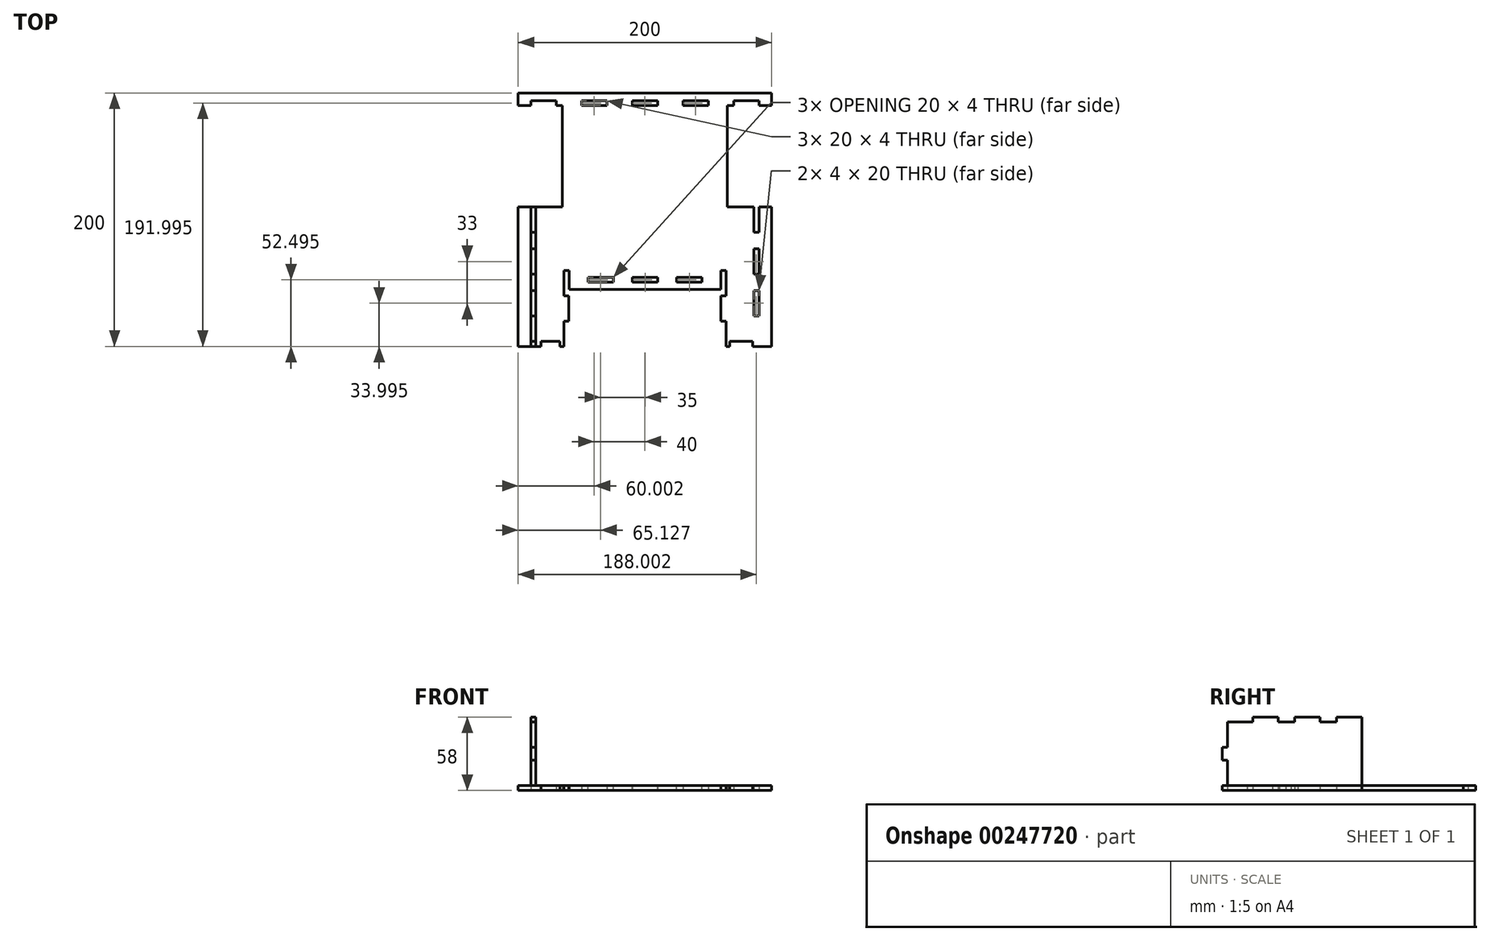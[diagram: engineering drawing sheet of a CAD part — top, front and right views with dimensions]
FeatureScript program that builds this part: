
annotation { "Feature Type Name" : "Feature", "Feature Type Description" : "" }
export const myFeature = defineFeature(function(context is Context, id is Id, definition is map)
    precondition{}
    {
        {
            var Q0;
            Q0=qCreatedBy(makeId("Top.planeOp"),FACE);
            var sketch = newSketch(context, id + "F0", { "sketchPlane" : qUnion([Q0])});
            skLineSegment(sketch, "E0.bottom", {"start": v(-157.98, 33.52) * mm, "end": v(42.02, 33.52) * mm});
            skLineSegment(sketch, "E0.top", {"start": v(-157.98, -166.48) * mm, "end": v(42.02, -166.48) * mm});
            skLineSegment(sketch, "E0.left", {"start": v(-157.98, 33.52) * mm, "end": v(-157.98, -166.48) * mm});
            skLineSegment(sketch, "E0.right", {"start": v(42.02, 33.52) * mm, "end": v(42.02, -166.48) * mm});
            skPoint(sketch, "E0.middle", {"position": v(-57.98, -66.48) * mm});
            skLineSegment(sketch, "E1", {"start": v(-57.98, -166.48) * mm, "end": v(-57.98, 18.52) * mm, "construction": true});
            skLineSegment(sketch, "E2", {"start": v(-57.98, 33.52) * mm, "end": v(-57.98, 27.52) * mm, "construction": true});
            skLineSegment(sketch, "E3.direction2", {"start": v(-47.98, 18.52) * mm, "end": v(-47.15, -161.48) * mm, "construction": true});
            skLineSegment(sketch, "E4", {"start": v(42.02, -66.48) * mm, "end": v(32.02, -66.48) * mm, "construction": true});
            skLineSegment(sketch, "E5", {"start": v(32.02, -66.48) * mm, "end": v(42.02, -66.48) * mm, "construction": true});
            skLineSegment(sketch, "E6.top", {"start": v(32.02, -76.48) * mm, "end": v(28.02, -76.48) * mm});
            skLineSegment(sketch, "E6.left", {"start": v(32.02, -66.48) * mm, "end": v(32.02, -76.48) * mm});
            skLineSegment(sketch, "E6.right", {"start": v(28.02, -66.48) * mm, "end": v(28.02, -76.48) * mm});
            skLineSegment(sketch, "E7.MirrorCS", {"start": v(28.02, -66.48) * mm, "end": v(28.02, -56.48) * mm});
            skLineSegment(sketch, "E8.MirrorCS", {"start": v(32.02, -66.48) * mm, "end": v(32.02, -56.48) * mm});
            skLineSegment(sketch, "E9.MirrorCS", {"start": v(32.02, -56.48) * mm, "end": v(28.02, -56.48) * mm});
            skLineSegment(sketch, "E10.trimOffspring", {"start": v(28.02, -66.48) * mm, "end": v(-157.98, -66.48) * mm, "construction": true});
            skLineSegment(sketch, "E11.direction1", {"start": v(28.02, -66.48) * mm, "end": v(52.02, -66.48) * mm, "construction": true});
            skLineSegment(sketch, "E11.direction2", {"start": v(28.02, -66.48) * mm, "end": v(28.02, -33.48) * mm, "construction": true});
            skLineSegment(sketch, "E12.MirrorCS", {"start": v(32.02, -99.48) * mm, "end": v(32.02, -109.48) * mm});
            skLineSegment(sketch, "E13.MirrorCS", {"start": v(32.02, -89.48) * mm, "end": v(28.02, -89.48) * mm});
            skLineSegment(sketch, "E14.MirrorCS", {"start": v(28.02, -99.48) * mm, "end": v(28.02, -89.48) * mm});
            skLineSegment(sketch, "E15.MirrorCS", {"start": v(28.02, -99.48) * mm, "end": v(28.02, -109.48) * mm});
            skLineSegment(sketch, "E16.MirrorCS", {"start": v(32.02, -99.48) * mm, "end": v(32.02, -89.48) * mm});
            skLineSegment(sketch, "E17.MirrorCS", {"start": v(32.02, -109.48) * mm, "end": v(28.02, -109.48) * mm});
            skLineSegment(sketch, "E18.MirrorCS", {"start": v(-147.98, -56.48) * mm, "end": v(-143.98, -56.48) * mm});
            skLineSegment(sketch, "E19.MirrorCS", {"start": v(-147.98, -99.48) * mm, "end": v(-147.98, -89.48) * mm});
            skLineSegment(sketch, "E20.MirrorCS", {"start": v(-147.98, -89.48) * mm, "end": v(-143.98, -89.48) * mm});
            skLineSegment(sketch, "E21.MirrorCS", {"start": v(-147.98, -76.48) * mm, "end": v(-143.98, -76.48) * mm});
            skLineSegment(sketch, "E22.MirrorCS", {"start": v(-147.98, -109.48) * mm, "end": v(-143.98, -109.48) * mm});
            skLineSegment(sketch, "E23.MirrorCS", {"start": v(-143.98, -99.48) * mm, "end": v(-143.98, -89.48) * mm});
            skLineSegment(sketch, "E24.MirrorCS", {"start": v(-143.98, -66.48) * mm, "end": v(-143.98, -56.48) * mm});
            skLineSegment(sketch, "E25.MirrorCS", {"start": v(-147.98, -99.48) * mm, "end": v(-147.98, -109.48) * mm});
            skLineSegment(sketch, "E26.MirrorCS", {"start": v(-143.98, -66.48) * mm, "end": v(-143.98, -33.48) * mm, "construction": true});
            skLineSegment(sketch, "E27.MirrorCS", {"start": v(-147.98, -66.48) * mm, "end": v(-147.98, -56.48) * mm});
            skLineSegment(sketch, "E28.MirrorCS", {"start": v(-143.98, -99.48) * mm, "end": v(-143.98, -109.48) * mm});
            skLineSegment(sketch, "E29.MirrorCS", {"start": v(-143.98, -66.48) * mm, "end": v(-143.98, -76.48) * mm});
            skLineSegment(sketch, "E30.MirrorCS", {"start": v(-147.98, -66.48) * mm, "end": v(-147.98, -76.48) * mm});
            skLineSegment(sketch, "E31.bottom", {"start": v(-57.98, 23.52) * mm, "end": v(-47.98, 23.52) * mm});
            skLineSegment(sketch, "E31.top", {"start": v(-57.98, 27.52) * mm, "end": v(-47.98, 27.52) * mm});
            skLineSegment(sketch, "E31.right", {"start": v(-47.98, 23.52) * mm, "end": v(-47.98, 27.52) * mm});
            skLineSegment(sketch, "E32.MirrorCS", {"start": v(-57.98, 27.52) * mm, "end": v(-67.98, 27.52) * mm});
            skLineSegment(sketch, "E33.MirrorCS", {"start": v(-67.98, 23.52) * mm, "end": v(-67.98, 27.52) * mm});
            skLineSegment(sketch, "E34.MirrorCS", {"start": v(-57.98, 23.52) * mm, "end": v(-67.98, 23.52) * mm});
            skPoint(sketch, "E35.orphan", {"position": v(-57.98, 23.52) * mm});
            skLineSegment(sketch, "E36.1.0.0", {"start": v(-17.98, 23.52) * mm, "end": v(-27.98, 23.52) * mm});
            skLineSegment(sketch, "E36.1.0.1", {"start": v(-27.98, 23.52) * mm, "end": v(-27.98, 27.52) * mm});
            skLineSegment(sketch, "E36.1.0.2", {"start": v(-7.98, 23.52) * mm, "end": v(-7.98, 27.52) * mm});
            skLineSegment(sketch, "E36.1.0.3", {"start": v(-17.98, 23.52) * mm, "end": v(-7.98, 23.52) * mm});
            skLineSegment(sketch, "E36.1.0.4", {"start": v(-17.98, 27.52) * mm, "end": v(-27.98, 27.52) * mm});
            skLineSegment(sketch, "E36.1.0.5", {"start": v(-17.98, 27.52) * mm, "end": v(-7.98, 27.52) * mm});
            skPoint(sketch, "E36.1.0.6", {"position": v(-17.98, 23.52) * mm});
            skLineSegment(sketch, "E36.2.0.0", {"start": v(22.02, 23.52) * mm, "end": v(12.02, 23.52) * mm});
            skLineSegment(sketch, "E36.2.0.1", {"start": v(12.02, 23.52) * mm, "end": v(12.02, 27.52) * mm});
            skLineSegment(sketch, "E36.2.0.2", {"start": v(32.02, 23.52) * mm, "end": v(32.02, 27.52) * mm});
            skLineSegment(sketch, "E36.2.0.3", {"start": v(22.02, 23.52) * mm, "end": v(32.02, 23.52) * mm});
            skLineSegment(sketch, "E36.2.0.4", {"start": v(22.02, 27.52) * mm, "end": v(12.02, 27.52) * mm});
            skLineSegment(sketch, "E36.2.0.5", {"start": v(22.02, 27.52) * mm, "end": v(32.02, 27.52) * mm});
            skPoint(sketch, "E36.2.0.6", {"position": v(22.02, 23.52) * mm});
            skLineSegment(sketch, "E36.direction1", {"start": v(-67.98, 23.52) * mm, "end": v(-27.98, 23.52) * mm, "construction": true});
            skPoint(sketch, "E37.MirrorP", {"position": v(-97.98, 23.52) * mm});
            skLineSegment(sketch, "E38.MirrorCS", {"start": v(-137.98, 23.52) * mm, "end": v(-147.98, 23.52) * mm});
            skLineSegment(sketch, "E39.MirrorCS", {"start": v(-97.98, 23.52) * mm, "end": v(-107.98, 23.52) * mm});
            skLineSegment(sketch, "E40.MirrorCS", {"start": v(-107.98, 23.52) * mm, "end": v(-107.98, 27.52) * mm});
            skLineSegment(sketch, "E41.MirrorCS", {"start": v(-137.98, 23.52) * mm, "end": v(-127.98, 23.52) * mm});
            skLineSegment(sketch, "E42.MirrorCS", {"start": v(-97.98, 27.52) * mm, "end": v(-107.98, 27.52) * mm});
            skLineSegment(sketch, "E43.MirrorCS", {"start": v(-97.98, 27.52) * mm, "end": v(-87.98, 27.52) * mm});
            skLineSegment(sketch, "E44.MirrorCS", {"start": v(-137.98, 27.52) * mm, "end": v(-147.98, 27.52) * mm});
            skLineSegment(sketch, "E45.MirrorCS", {"start": v(-137.98, 27.52) * mm, "end": v(-127.98, 27.52) * mm});
            skLineSegment(sketch, "E46.MirrorCS", {"start": v(-147.98, 23.52) * mm, "end": v(-147.98, 27.52) * mm});
            skPoint(sketch, "E47.MirrorP", {"position": v(-137.98, 23.52) * mm});
            skLineSegment(sketch, "E48.MirrorCS", {"start": v(-87.98, 23.52) * mm, "end": v(-87.98, 27.52) * mm});
            skLineSegment(sketch, "E49.MirrorCS", {"start": v(-127.98, 23.52) * mm, "end": v(-127.98, 27.52) * mm});
            skLineSegment(sketch, "E50.MirrorCS", {"start": v(-97.98, 23.52) * mm, "end": v(-87.98, 23.52) * mm});
            skLineSegment(sketch, "E51.MirrorCS", {"start": v(-143.98, -66.48) * mm, "end": v(42.02, -66.48) * mm, "construction": true});
            skLineSegment(sketch, "E52.MirrorCS", {"start": v(-143.98, -132.48) * mm, "end": v(-143.98, -122.48) * mm});
            skLineSegment(sketch, "E53.MirrorCS", {"start": v(-143.98, -132.48) * mm, "end": v(-143.98, -142.48) * mm});
            skLineSegment(sketch, "E54.MirrorCS", {"start": v(-147.98, -142.48) * mm, "end": v(-143.98, -142.48) * mm});
            skLineSegment(sketch, "E55.MirrorCS", {"start": v(-147.98, -132.48) * mm, "end": v(-147.98, -122.48) * mm});
            skLineSegment(sketch, "E56.MirrorCS", {"start": v(-147.98, -122.48) * mm, "end": v(-143.98, -122.48) * mm});
            skLineSegment(sketch, "E57.MirrorCS", {"start": v(-147.98, -132.48) * mm, "end": v(-147.98, -142.48) * mm});
            skLineSegment(sketch, "E58.MirrorCS", {"start": v(32.02, -132.48) * mm, "end": v(32.02, -142.48) * mm});
            skLineSegment(sketch, "E59.MirrorCS", {"start": v(32.02, -132.48) * mm, "end": v(32.02, -122.48) * mm});
            skLineSegment(sketch, "E60.MirrorCS", {"start": v(32.02, -122.48) * mm, "end": v(28.02, -122.48) * mm});
            skLineSegment(sketch, "E61.MirrorCS", {"start": v(28.02, -132.48) * mm, "end": v(28.02, -142.48) * mm});
            skLineSegment(sketch, "E62.MirrorCS", {"start": v(32.02, -142.48) * mm, "end": v(28.02, -142.48) * mm});
            skLineSegment(sketch, "E63.MirrorCS", {"start": v(28.02, -132.48) * mm, "end": v(28.02, -122.48) * mm});
            skSolve(sketch);
        }
        {
            var Q0;
            Q0 = qSketchRegion(id + "F0", true);
            extrude(context, id + "F1", {"entities" : qUnion([Q0]), "depth" : 4 * mm});
        }
        {
            var Q0;
            Q0=makeQuery(id+"F1.opExtrude","CAP_FACE",FACE,{"disambiguationData":[OSD([sQuery(id+"F0.wireOp",EDGE,"E0.bottom"),sQuery(id+"F0.wireOp",EDGE,"E0.top"),sQuery(id+"F0.wireOp",EDGE,"E0.left"),sQuery(id+"F0.wireOp",EDGE,"E0.right"),sQuery(id+"F0.wireOp",EDGE,"E6.top"),sQuery(id+"F0.wireOp",EDGE,"E6.left"),sQuery(id+"F0.wireOp",EDGE,"E6.right"),sQuery(id+"F0.wireOp",EDGE,"E7.MirrorCS"),sQuery(id+"F0.wireOp",EDGE,"E8.MirrorCS"),sQuery(id+"F0.wireOp",EDGE,"E9.MirrorCS"),sQuery(id+"F0.wireOp",EDGE,"E12.MirrorCS"),sQuery(id+"F0.wireOp",EDGE,"E13.MirrorCS"),sQuery(id+"F0.wireOp",EDGE,"E14.MirrorCS"),sQuery(id+"F0.wireOp",EDGE,"E15.MirrorCS"),sQuery(id+"F0.wireOp",EDGE,"E16.MirrorCS"),sQuery(id+"F0.wireOp",EDGE,"E17.MirrorCS"),sQuery(id+"F0.wireOp",EDGE,"E18.MirrorCS"),sQuery(id+"F0.wireOp",EDGE,"E19.MirrorCS"),sQuery(id+"F0.wireOp",EDGE,"E20.MirrorCS"),sQuery(id+"F0.wireOp",EDGE,"E21.MirrorCS"),sQuery(id+"F0.wireOp",EDGE,"E22.MirrorCS"),sQuery(id+"F0.wireOp",EDGE,"E23.MirrorCS"),sQuery(id+"F0.wireOp",EDGE,"E24.MirrorCS"),sQuery(id+"F0.wireOp",EDGE,"E25.MirrorCS"),sQuery(id+"F0.wireOp",EDGE,"E27.MirrorCS"),sQuery(id+"F0.wireOp",EDGE,"E28.MirrorCS"),sQuery(id+"F0.wireOp",EDGE,"E29.MirrorCS"),sQuery(id+"F0.wireOp",EDGE,"E30.MirrorCS"),sQuery(id+"F0.wireOp",EDGE,"E31.bottom"),sQuery(id+"F0.wireOp",EDGE,"E31.top"),sQuery(id+"F0.wireOp",EDGE,"E31.right"),sQuery(id+"F0.wireOp",EDGE,"E32.MirrorCS"),sQuery(id+"F0.wireOp",EDGE,"E33.MirrorCS"),sQuery(id+"F0.wireOp",EDGE,"E34.MirrorCS"),sQuery(id+"F0.wireOp",EDGE,"E36.1.0.0"),sQuery(id+"F0.wireOp",EDGE,"E36.1.0.1"),sQuery(id+"F0.wireOp",EDGE,"E36.1.0.2"),sQuery(id+"F0.wireOp",EDGE,"E36.1.0.3"),sQuery(id+"F0.wireOp",EDGE,"E36.1.0.4"),sQuery(id+"F0.wireOp",EDGE,"E36.1.0.5"),sQuery(id+"F0.wireOp",EDGE,"E36.2.0.0"),sQuery(id+"F0.wireOp",EDGE,"E36.2.0.1"),sQuery(id+"F0.wireOp",EDGE,"E36.2.0.2"),sQuery(id+"F0.wireOp",EDGE,"E36.2.0.3"),sQuery(id+"F0.wireOp",EDGE,"E36.2.0.4"),sQuery(id+"F0.wireOp",EDGE,"E36.2.0.5"),sQuery(id+"F0.wireOp",EDGE,"E38.MirrorCS"),sQuery(id+"F0.wireOp",EDGE,"E39.MirrorCS"),sQuery(id+"F0.wireOp",EDGE,"E40.MirrorCS"),sQuery(id+"F0.wireOp",EDGE,"E41.MirrorCS"),sQuery(id+"F0.wireOp",EDGE,"E42.MirrorCS"),sQuery(id+"F0.wireOp",EDGE,"E43.MirrorCS"),sQuery(id+"F0.wireOp",EDGE,"E44.MirrorCS"),sQuery(id+"F0.wireOp",EDGE,"E45.MirrorCS"),sQuery(id+"F0.wireOp",EDGE,"E46.MirrorCS"),sQuery(id+"F0.wireOp",EDGE,"E48.MirrorCS"),sQuery(id+"F0.wireOp",EDGE,"E49.MirrorCS"),sQuery(id+"F0.wireOp",EDGE,"E50.MirrorCS"),sQuery(id+"F0.wireOp",EDGE,"E52.MirrorCS"),sQuery(id+"F0.wireOp",EDGE,"E53.MirrorCS"),sQuery(id+"F0.wireOp",EDGE,"E54.MirrorCS"),sQuery(id+"F0.wireOp",EDGE,"E55.MirrorCS"),sQuery(id+"F0.wireOp",EDGE,"E56.MirrorCS"),sQuery(id+"F0.wireOp",EDGE,"E57.MirrorCS"),sQuery(id+"F0.wireOp",EDGE,"E60.MirrorCS"),sQuery(id+"F0.wireOp",EDGE,"E61.MirrorCS"),sQuery(id+"F0.wireOp",EDGE,"E58.MirrorCS"),sQuery(id+"F0.wireOp",EDGE,"E62.MirrorCS"),sQuery(id+"F0.wireOp",EDGE,"E59.MirrorCS"),sQuery(id+"F0.wireOp",EDGE,"E63.MirrorCS")])],"isStart":false});
            var sketch = newSketch(context, id + "F2", { "sketchPlane" : qUnion([Q0])});
            skLineSegment(sketch, "E64.bottom", {"start": v(-147.98, -56.48) * mm, "end": v(-143.98, -56.48) * mm});
            skLineSegment(sketch, "E64.top", {"start": v(-147.98, -76.48) * mm, "end": v(-143.98, -76.48) * mm});
            skLineSegment(sketch, "E64.left", {"start": v(-147.98, -56.48) * mm, "end": v(-147.98, -76.48) * mm});
            skLineSegment(sketch, "E64.right", {"start": v(-143.98, -56.48) * mm, "end": v(-143.98, -76.48) * mm});
            skLineSegment(sketch, "E65.0.1.0", {"start": v(-147.98, -21.48) * mm, "end": v(-143.98, -21.48) * mm});
            skLineSegment(sketch, "E65.0.1.1", {"start": v(-147.98, -41.48) * mm, "end": v(-143.98, -41.48) * mm});
            skLineSegment(sketch, "E65.0.1.2", {"start": v(-147.98, -21.48) * mm, "end": v(-147.98, -41.48) * mm});
            skLineSegment(sketch, "E65.0.1.3", {"start": v(-143.98, -21.48) * mm, "end": v(-143.98, -41.48) * mm});
            skLineSegment(sketch, "E65.0.2.0", {"start": v(-147.98, 13.52) * mm, "end": v(-143.98, 13.52) * mm});
            skLineSegment(sketch, "E65.0.2.1", {"start": v(-147.98, -6.48) * mm, "end": v(-143.98, -6.48) * mm});
            skLineSegment(sketch, "E65.0.2.2", {"start": v(-147.98, 13.52) * mm, "end": v(-147.98, -6.48) * mm});
            skLineSegment(sketch, "E65.0.2.3", {"start": v(-143.98, 13.52) * mm, "end": v(-143.98, -6.48) * mm});
            skLineSegment(sketch, "E65.direction1", {"start": v(-147.98, -76.48) * mm, "end": v(-172.98, -76.48) * mm, "construction": true});
            skLineSegment(sketch, "E65.direction2", {"start": v(-147.98, -76.48) * mm, "end": v(-147.98, -41.48) * mm, "construction": true});
            skLineSegment(sketch, "E66.bottom", {"start": v(-147.98, -89.48) * mm, "end": v(-143.98, -89.48) * mm});
            skLineSegment(sketch, "E66.top", {"start": v(-147.98, -109.48) * mm, "end": v(-143.98, -109.48) * mm});
            skLineSegment(sketch, "E66.left", {"start": v(-147.98, -89.48) * mm, "end": v(-147.98, -109.48) * mm});
            skLineSegment(sketch, "E66.right", {"start": v(-143.98, -89.48) * mm, "end": v(-143.98, -109.48) * mm});
            skLineSegment(sketch, "E67.bottom", {"start": v(-147.98, -122.48) * mm, "end": v(-143.98, -122.48) * mm});
            skLineSegment(sketch, "E67.top", {"start": v(-147.98, -142.48) * mm, "end": v(-143.98, -142.48) * mm});
            skLineSegment(sketch, "E67.left", {"start": v(-147.98, -122.48) * mm, "end": v(-147.98, -142.48) * mm});
            skLineSegment(sketch, "E67.right", {"start": v(-143.98, -122.48) * mm, "end": v(-143.98, -142.48) * mm});
            skSolve(sketch);
        }
        {
            var Q0;
            Q0 = qSketchRegion(id + "F2", true);
            extrude(context, id + "F3", {"entities" : qUnion([Q0]), "depth" : 54 * mm});
        }
        {
            var Q0;
            Q0=makeQuery(id+"F1.opExtrude","CAP_FACE",FACE,{"disambiguationData":[OSD([sQuery(id+"F0.wireOp",EDGE,"E0.bottom"),sQuery(id+"F0.wireOp",EDGE,"E0.top"),sQuery(id+"F0.wireOp",EDGE,"E0.left"),sQuery(id+"F0.wireOp",EDGE,"E0.right"),sQuery(id+"F0.wireOp",EDGE,"E6.top"),sQuery(id+"F0.wireOp",EDGE,"E6.left"),sQuery(id+"F0.wireOp",EDGE,"E6.right"),sQuery(id+"F0.wireOp",EDGE,"E7.MirrorCS"),sQuery(id+"F0.wireOp",EDGE,"E8.MirrorCS"),sQuery(id+"F0.wireOp",EDGE,"E9.MirrorCS"),sQuery(id+"F0.wireOp",EDGE,"E12.MirrorCS"),sQuery(id+"F0.wireOp",EDGE,"E13.MirrorCS"),sQuery(id+"F0.wireOp",EDGE,"E14.MirrorCS"),sQuery(id+"F0.wireOp",EDGE,"E15.MirrorCS"),sQuery(id+"F0.wireOp",EDGE,"E16.MirrorCS"),sQuery(id+"F0.wireOp",EDGE,"E17.MirrorCS"),sQuery(id+"F0.wireOp",EDGE,"E18.MirrorCS"),sQuery(id+"F0.wireOp",EDGE,"E19.MirrorCS"),sQuery(id+"F0.wireOp",EDGE,"E20.MirrorCS"),sQuery(id+"F0.wireOp",EDGE,"E21.MirrorCS"),sQuery(id+"F0.wireOp",EDGE,"E22.MirrorCS"),sQuery(id+"F0.wireOp",EDGE,"E23.MirrorCS"),sQuery(id+"F0.wireOp",EDGE,"E24.MirrorCS"),sQuery(id+"F0.wireOp",EDGE,"E25.MirrorCS"),sQuery(id+"F0.wireOp",EDGE,"E27.MirrorCS"),sQuery(id+"F0.wireOp",EDGE,"E28.MirrorCS"),sQuery(id+"F0.wireOp",EDGE,"E29.MirrorCS"),sQuery(id+"F0.wireOp",EDGE,"E30.MirrorCS"),sQuery(id+"F0.wireOp",EDGE,"E31.bottom"),sQuery(id+"F0.wireOp",EDGE,"E31.top"),sQuery(id+"F0.wireOp",EDGE,"E31.right"),sQuery(id+"F0.wireOp",EDGE,"E32.MirrorCS"),sQuery(id+"F0.wireOp",EDGE,"E33.MirrorCS"),sQuery(id+"F0.wireOp",EDGE,"E34.MirrorCS"),sQuery(id+"F0.wireOp",EDGE,"E36.1.0.0"),sQuery(id+"F0.wireOp",EDGE,"E36.1.0.1"),sQuery(id+"F0.wireOp",EDGE,"E36.1.0.2"),sQuery(id+"F0.wireOp",EDGE,"E36.1.0.3"),sQuery(id+"F0.wireOp",EDGE,"E36.1.0.4"),sQuery(id+"F0.wireOp",EDGE,"E36.1.0.5"),sQuery(id+"F0.wireOp",EDGE,"E36.2.0.0"),sQuery(id+"F0.wireOp",EDGE,"E36.2.0.1"),sQuery(id+"F0.wireOp",EDGE,"E36.2.0.2"),sQuery(id+"F0.wireOp",EDGE,"E36.2.0.3"),sQuery(id+"F0.wireOp",EDGE,"E36.2.0.4"),sQuery(id+"F0.wireOp",EDGE,"E36.2.0.5"),sQuery(id+"F0.wireOp",EDGE,"E38.MirrorCS"),sQuery(id+"F0.wireOp",EDGE,"E39.MirrorCS"),sQuery(id+"F0.wireOp",EDGE,"E40.MirrorCS"),sQuery(id+"F0.wireOp",EDGE,"E41.MirrorCS"),sQuery(id+"F0.wireOp",EDGE,"E42.MirrorCS"),sQuery(id+"F0.wireOp",EDGE,"E43.MirrorCS"),sQuery(id+"F0.wireOp",EDGE,"E44.MirrorCS"),sQuery(id+"F0.wireOp",EDGE,"E45.MirrorCS"),sQuery(id+"F0.wireOp",EDGE,"E46.MirrorCS"),sQuery(id+"F0.wireOp",EDGE,"E48.MirrorCS"),sQuery(id+"F0.wireOp",EDGE,"E49.MirrorCS"),sQuery(id+"F0.wireOp",EDGE,"E50.MirrorCS"),sQuery(id+"F0.wireOp",EDGE,"E52.MirrorCS"),sQuery(id+"F0.wireOp",EDGE,"E53.MirrorCS"),sQuery(id+"F0.wireOp",EDGE,"E54.MirrorCS"),sQuery(id+"F0.wireOp",EDGE,"E55.MirrorCS"),sQuery(id+"F0.wireOp",EDGE,"E56.MirrorCS"),sQuery(id+"F0.wireOp",EDGE,"E57.MirrorCS"),sQuery(id+"F0.wireOp",EDGE,"E60.MirrorCS"),sQuery(id+"F0.wireOp",EDGE,"E61.MirrorCS"),sQuery(id+"F0.wireOp",EDGE,"E58.MirrorCS"),sQuery(id+"F0.wireOp",EDGE,"E62.MirrorCS"),sQuery(id+"F0.wireOp",EDGE,"E59.MirrorCS"),sQuery(id+"F0.wireOp",EDGE,"E63.MirrorCS")])],"isStart":false});
            var sketch = newSketch(context, id + "F4", { "sketchPlane" : qUnion([Q0])});
            skLineSegment(sketch, "E68", {"start": v(-157.98, -66.48) * mm, "end": v(42.02, -66.48) * mm, "construction": true});
            skLineSegment(sketch, "E69", {"start": v(-57.98, -166.48) * mm, "end": v(-57.98, 33.52) * mm, "construction": true});
            skPoint(sketch, "E70", {"position": v(-57.98, -66.48) * mm});
            skLineSegment(sketch, "E71.bottom", {"start": v(-57.98, -166.48) * mm, "end": v(-117.98, -166.48) * mm});
            skLineSegment(sketch, "E71.top", {"start": v(-57.98, -121.48) * mm, "end": v(-117.98, -121.48) * mm});
            skLineSegment(sketch, "E71.left", {"start": v(-57.98, -166.48) * mm, "end": v(-57.98, -121.48) * mm});
            skLineSegment(sketch, "E71.right", {"start": v(-117.98, -166.48) * mm, "end": v(-117.98, -121.48) * mm});
            skLineSegment(sketch, "E72.MirrorCS", {"start": v(-57.98, -121.48) * mm, "end": v(2.02, -121.48) * mm});
            skLineSegment(sketch, "E73.MirrorCS", {"start": v(2.02, -166.48) * mm, "end": v(2.02, -121.48) * mm});
            skLineSegment(sketch, "E74", {"start": v(-117.98, -166.48) * mm, "end": v(2.02, -166.48) * mm});
            skSolve(sketch);
        }
        {
            var Q0;
            Q0 = qSketchRegion(id + "F4", true);
            extrude(context, id + "F5", {"entities" : qUnion([Q0]), "operationType" : NewBodyOperationType.REMOVE, "oppositeDirection" : true, "depth" : 25 * mm});
        }
        {
            var Q0;
            Q0=makeQuery(id+"F1.opExtrude","CAP_FACE",FACE,{"disambiguationData":[OSD([sQuery(id+"F0.wireOp",EDGE,"E0.bottom"),sQuery(id+"F0.wireOp",EDGE,"E0.top"),sQuery(id+"F0.wireOp",EDGE,"E0.left"),sQuery(id+"F0.wireOp",EDGE,"E0.right"),sQuery(id+"F0.wireOp",EDGE,"E6.top"),sQuery(id+"F0.wireOp",EDGE,"E6.left"),sQuery(id+"F0.wireOp",EDGE,"E6.right"),sQuery(id+"F0.wireOp",EDGE,"E7.MirrorCS"),sQuery(id+"F0.wireOp",EDGE,"E8.MirrorCS"),sQuery(id+"F0.wireOp",EDGE,"E9.MirrorCS"),sQuery(id+"F0.wireOp",EDGE,"E12.MirrorCS"),sQuery(id+"F0.wireOp",EDGE,"E13.MirrorCS"),sQuery(id+"F0.wireOp",EDGE,"E14.MirrorCS"),sQuery(id+"F0.wireOp",EDGE,"E15.MirrorCS"),sQuery(id+"F0.wireOp",EDGE,"E16.MirrorCS"),sQuery(id+"F0.wireOp",EDGE,"E17.MirrorCS"),sQuery(id+"F0.wireOp",EDGE,"E18.MirrorCS"),sQuery(id+"F0.wireOp",EDGE,"E19.MirrorCS"),sQuery(id+"F0.wireOp",EDGE,"E20.MirrorCS"),sQuery(id+"F0.wireOp",EDGE,"E21.MirrorCS"),sQuery(id+"F0.wireOp",EDGE,"E22.MirrorCS"),sQuery(id+"F0.wireOp",EDGE,"E23.MirrorCS"),sQuery(id+"F0.wireOp",EDGE,"E24.MirrorCS"),sQuery(id+"F0.wireOp",EDGE,"E25.MirrorCS"),sQuery(id+"F0.wireOp",EDGE,"E27.MirrorCS"),sQuery(id+"F0.wireOp",EDGE,"E28.MirrorCS"),sQuery(id+"F0.wireOp",EDGE,"E29.MirrorCS"),sQuery(id+"F0.wireOp",EDGE,"E30.MirrorCS"),sQuery(id+"F0.wireOp",EDGE,"E31.bottom"),sQuery(id+"F0.wireOp",EDGE,"E31.top"),sQuery(id+"F0.wireOp",EDGE,"E31.right"),sQuery(id+"F0.wireOp",EDGE,"E32.MirrorCS"),sQuery(id+"F0.wireOp",EDGE,"E33.MirrorCS"),sQuery(id+"F0.wireOp",EDGE,"E34.MirrorCS"),sQuery(id+"F0.wireOp",EDGE,"E36.1.0.0"),sQuery(id+"F0.wireOp",EDGE,"E36.1.0.1"),sQuery(id+"F0.wireOp",EDGE,"E36.1.0.2"),sQuery(id+"F0.wireOp",EDGE,"E36.1.0.3"),sQuery(id+"F0.wireOp",EDGE,"E36.1.0.4"),sQuery(id+"F0.wireOp",EDGE,"E36.1.0.5"),sQuery(id+"F0.wireOp",EDGE,"E36.2.0.0"),sQuery(id+"F0.wireOp",EDGE,"E36.2.0.1"),sQuery(id+"F0.wireOp",EDGE,"E36.2.0.2"),sQuery(id+"F0.wireOp",EDGE,"E36.2.0.3"),sQuery(id+"F0.wireOp",EDGE,"E36.2.0.4"),sQuery(id+"F0.wireOp",EDGE,"E36.2.0.5"),sQuery(id+"F0.wireOp",EDGE,"E38.MirrorCS"),sQuery(id+"F0.wireOp",EDGE,"E39.MirrorCS"),sQuery(id+"F0.wireOp",EDGE,"E40.MirrorCS"),sQuery(id+"F0.wireOp",EDGE,"E41.MirrorCS"),sQuery(id+"F0.wireOp",EDGE,"E42.MirrorCS"),sQuery(id+"F0.wireOp",EDGE,"E43.MirrorCS"),sQuery(id+"F0.wireOp",EDGE,"E44.MirrorCS"),sQuery(id+"F0.wireOp",EDGE,"E45.MirrorCS"),sQuery(id+"F0.wireOp",EDGE,"E46.MirrorCS"),sQuery(id+"F0.wireOp",EDGE,"E48.MirrorCS"),sQuery(id+"F0.wireOp",EDGE,"E49.MirrorCS"),sQuery(id+"F0.wireOp",EDGE,"E50.MirrorCS"),sQuery(id+"F0.wireOp",EDGE,"E52.MirrorCS"),sQuery(id+"F0.wireOp",EDGE,"E53.MirrorCS"),sQuery(id+"F0.wireOp",EDGE,"E54.MirrorCS"),sQuery(id+"F0.wireOp",EDGE,"E55.MirrorCS"),sQuery(id+"F0.wireOp",EDGE,"E56.MirrorCS"),sQuery(id+"F0.wireOp",EDGE,"E57.MirrorCS"),sQuery(id+"F0.wireOp",EDGE,"E60.MirrorCS"),sQuery(id+"F0.wireOp",EDGE,"E61.MirrorCS"),sQuery(id+"F0.wireOp",EDGE,"E58.MirrorCS"),sQuery(id+"F0.wireOp",EDGE,"E62.MirrorCS"),sQuery(id+"F0.wireOp",EDGE,"E59.MirrorCS"),sQuery(id+"F0.wireOp",EDGE,"E63.MirrorCS")])],"isStart":true});
            var sketch = newSketch(context, id + "F6", { "sketchPlane" : qUnion([Q0])});
            skLineSegment(sketch, "E75.bottom", {"start": v(-147.98, 56.48) * mm, "end": v(-143.98, 56.48) * mm});
            skLineSegment(sketch, "E75.top", {"start": v(-147.98, 76.48) * mm, "end": v(-143.98, 76.48) * mm});
            skLineSegment(sketch, "E75.left", {"start": v(-147.98, 56.48) * mm, "end": v(-147.98, 76.48) * mm});
            skLineSegment(sketch, "E75.right", {"start": v(-143.98, 56.48) * mm, "end": v(-143.98, 76.48) * mm});
            skLineSegment(sketch, "E76.bottom", {"start": v(-147.98, 89.48) * mm, "end": v(-143.98, 89.48) * mm});
            skLineSegment(sketch, "E76.top", {"start": v(-147.98, 109.48) * mm, "end": v(-143.98, 109.48) * mm});
            skLineSegment(sketch, "E76.left", {"start": v(-147.98, 89.48) * mm, "end": v(-147.98, 109.48) * mm});
            skLineSegment(sketch, "E76.right", {"start": v(-143.98, 89.48) * mm, "end": v(-143.98, 109.48) * mm});
            skLineSegment(sketch, "E77.bottom", {"start": v(-147.98, 122.48) * mm, "end": v(-143.98, 122.48) * mm});
            skLineSegment(sketch, "E77.top", {"start": v(-147.98, 142.48) * mm, "end": v(-143.98, 142.48) * mm});
            skLineSegment(sketch, "E77.left", {"start": v(-147.98, 122.48) * mm, "end": v(-147.98, 142.48) * mm});
            skLineSegment(sketch, "E77.right", {"start": v(-143.98, 122.48) * mm, "end": v(-143.98, 142.48) * mm});
            skSolve(sketch);
        }
        {
            var Q0;
            Q0 = qSketchRegion(id + "F6", true);
            extrude(context, id + "F7", {"entities" : qUnion([Q0]), "oppositeDirection" : true, "depth" : 4 * mm});
        }
        {
            var Q0;
            Q0=makeQuery(id+"F3.opExtrude","SWEPT_BODY",BODY,{"disambiguationData":[OSD([sQuery(id+"F2.wireOp",EDGE,"E66.bottom"),sQuery(id+"F2.wireOp",EDGE,"E66.top"),sQuery(id+"F2.wireOp",EDGE,"E66.left"),sQuery(id+"F2.wireOp",EDGE,"E66.right")])]});
            var Q1;
            Q1=makeQuery(id+"F7.opExtrude","SWEPT_BODY",BODY,{"disambiguationData":[OSD([sQuery(id+"F6.wireOp",EDGE,"E76.bottom"),sQuery(id+"F6.wireOp",EDGE,"E76.top"),sQuery(id+"F6.wireOp",EDGE,"E76.left"),sQuery(id+"F6.wireOp",EDGE,"E76.right")])]});
            booleanBodies(context, id + "F8", {"operationType" : BooleanOperationType.UNION, "tools" : qUnion([Q0, Q1])});
        }
        {
            var Q0;
            Q0=makeQuery(id+"F3.opExtrude","SWEPT_BODY",BODY,{"disambiguationData":[OSD([sQuery(id+"F2.wireOp",EDGE,"E67.bottom"),sQuery(id+"F2.wireOp",EDGE,"E67.top"),sQuery(id+"F2.wireOp",EDGE,"E67.left"),sQuery(id+"F2.wireOp",EDGE,"E67.right")])]});
            var Q1;
            Q1=makeQuery(id+"F7.opExtrude","SWEPT_BODY",BODY,{"disambiguationData":[OSD([sQuery(id+"F6.wireOp",EDGE,"E77.bottom"),sQuery(id+"F6.wireOp",EDGE,"E77.top"),sQuery(id+"F6.wireOp",EDGE,"E77.left"),sQuery(id+"F6.wireOp",EDGE,"E77.right")])]});
            booleanBodies(context, id + "F9", {"operationType" : BooleanOperationType.UNION, "tools" : qUnion([Q0, Q1])});
        }
        {
            var Q0;
            Q0=makeQuery(id+"F3.opExtrude","SWEPT_BODY",BODY,{"disambiguationData":[OSD([sQuery(id+"F2.wireOp",EDGE,"E64.bottom"),sQuery(id+"F2.wireOp",EDGE,"E64.top"),sQuery(id+"F2.wireOp",EDGE,"E64.left"),sQuery(id+"F2.wireOp",EDGE,"E64.right")])]});
            var Q1;
            Q1=makeQuery(id+"F7.opExtrude","SWEPT_BODY",BODY,{"disambiguationData":[OSD([sQuery(id+"F6.wireOp",EDGE,"E75.bottom"),sQuery(id+"F6.wireOp",EDGE,"E75.top"),sQuery(id+"F6.wireOp",EDGE,"E75.left"),sQuery(id+"F6.wireOp",EDGE,"E75.right")])]});
            booleanBodies(context, id + "F10", {"operationType" : BooleanOperationType.UNION, "tools" : qUnion([Q0, Q1])});
        }
        {
            var Q0;
            Q0=makeQuery(id+"F1.opExtrude","CAP_FACE",FACE,{"disambiguationData":[OSD([sQuery(id+"F0.wireOp",EDGE,"E0.bottom"),sQuery(id+"F0.wireOp",EDGE,"E0.top"),sQuery(id+"F0.wireOp",EDGE,"E0.left"),sQuery(id+"F0.wireOp",EDGE,"E0.right"),sQuery(id+"F0.wireOp",EDGE,"E6.top"),sQuery(id+"F0.wireOp",EDGE,"E6.left"),sQuery(id+"F0.wireOp",EDGE,"E6.right"),sQuery(id+"F0.wireOp",EDGE,"E7.MirrorCS"),sQuery(id+"F0.wireOp",EDGE,"E8.MirrorCS"),sQuery(id+"F0.wireOp",EDGE,"E9.MirrorCS"),sQuery(id+"F0.wireOp",EDGE,"E12.MirrorCS"),sQuery(id+"F0.wireOp",EDGE,"E13.MirrorCS"),sQuery(id+"F0.wireOp",EDGE,"E14.MirrorCS"),sQuery(id+"F0.wireOp",EDGE,"E15.MirrorCS"),sQuery(id+"F0.wireOp",EDGE,"E16.MirrorCS"),sQuery(id+"F0.wireOp",EDGE,"E17.MirrorCS"),sQuery(id+"F0.wireOp",EDGE,"E18.MirrorCS"),sQuery(id+"F0.wireOp",EDGE,"E19.MirrorCS"),sQuery(id+"F0.wireOp",EDGE,"E20.MirrorCS"),sQuery(id+"F0.wireOp",EDGE,"E21.MirrorCS"),sQuery(id+"F0.wireOp",EDGE,"E22.MirrorCS"),sQuery(id+"F0.wireOp",EDGE,"E23.MirrorCS"),sQuery(id+"F0.wireOp",EDGE,"E24.MirrorCS"),sQuery(id+"F0.wireOp",EDGE,"E25.MirrorCS"),sQuery(id+"F0.wireOp",EDGE,"E27.MirrorCS"),sQuery(id+"F0.wireOp",EDGE,"E28.MirrorCS"),sQuery(id+"F0.wireOp",EDGE,"E29.MirrorCS"),sQuery(id+"F0.wireOp",EDGE,"E30.MirrorCS"),sQuery(id+"F0.wireOp",EDGE,"E31.bottom"),sQuery(id+"F0.wireOp",EDGE,"E31.top"),sQuery(id+"F0.wireOp",EDGE,"E31.right"),sQuery(id+"F0.wireOp",EDGE,"E32.MirrorCS"),sQuery(id+"F0.wireOp",EDGE,"E33.MirrorCS"),sQuery(id+"F0.wireOp",EDGE,"E34.MirrorCS"),sQuery(id+"F0.wireOp",EDGE,"E36.1.0.0"),sQuery(id+"F0.wireOp",EDGE,"E36.1.0.1"),sQuery(id+"F0.wireOp",EDGE,"E36.1.0.2"),sQuery(id+"F0.wireOp",EDGE,"E36.1.0.3"),sQuery(id+"F0.wireOp",EDGE,"E36.1.0.4"),sQuery(id+"F0.wireOp",EDGE,"E36.1.0.5"),sQuery(id+"F0.wireOp",EDGE,"E36.2.0.0"),sQuery(id+"F0.wireOp",EDGE,"E36.2.0.1"),sQuery(id+"F0.wireOp",EDGE,"E36.2.0.2"),sQuery(id+"F0.wireOp",EDGE,"E36.2.0.3"),sQuery(id+"F0.wireOp",EDGE,"E36.2.0.4"),sQuery(id+"F0.wireOp",EDGE,"E36.2.0.5"),sQuery(id+"F0.wireOp",EDGE,"E38.MirrorCS"),sQuery(id+"F0.wireOp",EDGE,"E39.MirrorCS"),sQuery(id+"F0.wireOp",EDGE,"E40.MirrorCS"),sQuery(id+"F0.wireOp",EDGE,"E41.MirrorCS"),sQuery(id+"F0.wireOp",EDGE,"E42.MirrorCS"),sQuery(id+"F0.wireOp",EDGE,"E43.MirrorCS"),sQuery(id+"F0.wireOp",EDGE,"E44.MirrorCS"),sQuery(id+"F0.wireOp",EDGE,"E45.MirrorCS"),sQuery(id+"F0.wireOp",EDGE,"E46.MirrorCS"),sQuery(id+"F0.wireOp",EDGE,"E48.MirrorCS"),sQuery(id+"F0.wireOp",EDGE,"E49.MirrorCS"),sQuery(id+"F0.wireOp",EDGE,"E50.MirrorCS"),sQuery(id+"F0.wireOp",EDGE,"E52.MirrorCS"),sQuery(id+"F0.wireOp",EDGE,"E53.MirrorCS"),sQuery(id+"F0.wireOp",EDGE,"E54.MirrorCS"),sQuery(id+"F0.wireOp",EDGE,"E55.MirrorCS"),sQuery(id+"F0.wireOp",EDGE,"E56.MirrorCS"),sQuery(id+"F0.wireOp",EDGE,"E57.MirrorCS"),sQuery(id+"F0.wireOp",EDGE,"E60.MirrorCS"),sQuery(id+"F0.wireOp",EDGE,"E61.MirrorCS"),sQuery(id+"F0.wireOp",EDGE,"E58.MirrorCS"),sQuery(id+"F0.wireOp",EDGE,"E62.MirrorCS"),sQuery(id+"F0.wireOp",EDGE,"E59.MirrorCS"),sQuery(id+"F0.wireOp",EDGE,"E63.MirrorCS")])],"isStart":false});
            var sketch = newSketch(context, id + "F11", { "sketchPlane" : qUnion([Q0])});
            skPoint(sketch, "E78.0", {"position": v(-147.98, 13.52) * mm});
            skPoint(sketch, "E79.0", {"position": v(-143.98, -142.48) * mm});
            skLineSegment(sketch, "E80.bottom", {"start": v(-147.98, 13.52) * mm, "end": v(-143.98, 13.52) * mm});
            skLineSegment(sketch, "E80.top", {"start": v(-147.98, -162.48) * mm, "end": v(-143.98, -162.48) * mm});
            skLineSegment(sketch, "E80.left", {"start": v(-147.98, 13.52) * mm, "end": v(-147.98, -162.48) * mm});
            skLineSegment(sketch, "E80.right", {"start": v(-143.98, 13.52) * mm, "end": v(-143.98, -162.48) * mm});
            skSolve(sketch);
        }
        {
            var Q0;
            Q0 = qSketchRegion(id + "F11", true);
            extrude(context, id + "F12", {"entities" : qUnion([Q0]), "operationType" : NewBodyOperationType.ADD, "depth" : 50 * mm});
        }
        {
            var Q0;
            Q0=makeQuery(id+"F12.boolean.opBoolean","MERGE",FACE,{"derivedFrom":[makeQuery(id+"F3.opExtrude","SWEPT_FACE",FACE,{"disambiguationData":[OSD([sQuery(id+"F2.wireOp",EDGE,"E65.0.1.2")])]}),makeQuery(id+"F3.opExtrude","SWEPT_FACE",FACE,{"disambiguationData":[OSD([sQuery(id+"F2.wireOp",EDGE,"E65.0.2.2")])]}),makeQuery(id+"F8.opBoolean","MERGE",FACE,{"derivedFrom":[makeQuery(id+"F3.opExtrude","SWEPT_FACE",FACE,{"disambiguationData":[OSD([sQuery(id+"F2.wireOp",EDGE,"E66.left")])]}),makeQuery(id+"F7.opExtrude","SWEPT_FACE",FACE,{"disambiguationData":[OSD([sQuery(id+"F6.wireOp",EDGE,"E76.left")])]})]}),makeQuery(id+"F9.opBoolean","MERGE",FACE,{"derivedFrom":[makeQuery(id+"F3.opExtrude","SWEPT_FACE",FACE,{"disambiguationData":[OSD([sQuery(id+"F2.wireOp",EDGE,"E67.left")])]}),makeQuery(id+"F7.opExtrude","SWEPT_FACE",FACE,{"disambiguationData":[OSD([sQuery(id+"F6.wireOp",EDGE,"E77.left")])]})]}),makeQuery(id+"F10.opBoolean","MERGE",FACE,{"derivedFrom":[makeQuery(id+"F3.opExtrude","SWEPT_FACE",FACE,{"disambiguationData":[OSD([sQuery(id+"F2.wireOp",EDGE,"E64.left")])]}),makeQuery(id+"F7.opExtrude","SWEPT_FACE",FACE,{"disambiguationData":[OSD([sQuery(id+"F6.wireOp",EDGE,"E75.left")])]})]}),makeQuery(id+"F12.opExtrude","SWEPT_FACE",FACE,{"disambiguationData":[OSD([sQuery(id+"F11.wireOp",EDGE,"vlh3IDmt-7TSj-wOBe-oZ9h-uO47jx5dVmEl.left")])]})]});
            var sketch = newSketch(context, id + "F13", { "sketchPlane" : qUnion([Q0])});
            skLineSegment(sketch, "E81.bottom", {"start": v(-13.52, 4) * mm, "end": v(56.48, 4) * mm});
            skLineSegment(sketch, "E81.top", {"start": v(-13.52, 27) * mm, "end": v(56.48, 27) * mm});
            skLineSegment(sketch, "E81.left", {"start": v(-13.52, 4) * mm, "end": v(-13.52, 27) * mm});
            skLineSegment(sketch, "E81.right", {"start": v(56.48, 4) * mm, "end": v(56.48, 27) * mm});
            skSolve(sketch);
        }
        {
            var Q0;
            Q0 = qSketchRegion(id + "F13", true);
            var Q1;
            Q1=makeQuery(id+"F12.boolean.opBoolean","MERGE",FACE,{"derivedFrom":[makeQuery(id+"F3.opExtrude","SWEPT_FACE",FACE,{"disambiguationData":[OSD([sQuery(id+"F2.wireOp",EDGE,"E65.0.1.3")])]}),makeQuery(id+"F3.opExtrude","SWEPT_FACE",FACE,{"disambiguationData":[OSD([sQuery(id+"F2.wireOp",EDGE,"E65.0.2.3")])]}),makeQuery(id+"F8.opBoolean","MERGE",FACE,{"derivedFrom":[makeQuery(id+"F3.opExtrude","SWEPT_FACE",FACE,{"disambiguationData":[OSD([sQuery(id+"F2.wireOp",EDGE,"E66.right")])]}),makeQuery(id+"F7.opExtrude","SWEPT_FACE",FACE,{"disambiguationData":[OSD([sQuery(id+"F6.wireOp",EDGE,"E76.right")])]})]}),makeQuery(id+"F9.opBoolean","MERGE",FACE,{"derivedFrom":[makeQuery(id+"F3.opExtrude","SWEPT_FACE",FACE,{"disambiguationData":[OSD([sQuery(id+"F2.wireOp",EDGE,"E67.right")])]}),makeQuery(id+"F7.opExtrude","SWEPT_FACE",FACE,{"disambiguationData":[OSD([sQuery(id+"F6.wireOp",EDGE,"E77.right")])]})]}),makeQuery(id+"F10.opBoolean","MERGE",FACE,{"derivedFrom":[makeQuery(id+"F3.opExtrude","SWEPT_FACE",FACE,{"disambiguationData":[OSD([sQuery(id+"F2.wireOp",EDGE,"E64.right")])]}),makeQuery(id+"F7.opExtrude","SWEPT_FACE",FACE,{"disambiguationData":[OSD([sQuery(id+"F6.wireOp",EDGE,"E75.right")])]})]}),makeQuery(id+"F12.opExtrude","SWEPT_FACE",FACE,{"disambiguationData":[OSD([sQuery(id+"F11.wireOp",EDGE,"vlh3IDmt-7TSj-wOBe-oZ9h-uO47jx5dVmEl.right")])]})]});
            extrude(context, id + "F14", {"entities" : qUnion([Q0]), "operationType" : NewBodyOperationType.REMOVE, "endBound" : BoundingType.UP_TO_SURFACE, "oppositeDirection" : true, "endBoundEntityFace" : qUnion([Q1]), "depth" : 25 * mm});
        }
        {
            var Q0;
            Q0=makeQuery(id+"F12.opExtrude","SWEPT_FACE",FACE,{"disambiguationData":[OSD([sQuery(id+"F11.wireOp",EDGE,"E80.top")])]});
            var sketch = newSketch(context, id + "F15", { "sketchPlane" : qUnion([Q0])});
            skPoint(sketch, "E82", {"position": v(-147.98, 29) * mm});
            skPoint(sketch, "E83", {"position": v(-143.98, 29) * mm});
            skLineSegment(sketch, "E84.bottom", {"start": v(-147.98, 29) * mm, "end": v(-143.98, 29) * mm});
            skLineSegment(sketch, "E84.top", {"start": v(-147.98, 34) * mm, "end": v(-143.98, 34) * mm});
            skLineSegment(sketch, "E84.left", {"start": v(-147.98, 29) * mm, "end": v(-147.98, 34) * mm});
            skLineSegment(sketch, "E84.right", {"start": v(-143.98, 29) * mm, "end": v(-143.98, 34) * mm});
            skLineSegment(sketch, "E85.MirrorCS", {"start": v(-147.98, 24) * mm, "end": v(-143.98, 24) * mm});
            skLineSegment(sketch, "E86.MirrorCS", {"start": v(-147.98, 29) * mm, "end": v(-147.98, 24) * mm});
            skLineSegment(sketch, "E87.MirrorCS", {"start": v(-143.98, 29) * mm, "end": v(-143.98, 24) * mm});
            skSolve(sketch);
        }
        {
            var Q0;
            Q0 = qSketchRegion(id + "F15", true);
            extrude(context, id + "F16", {"entities" : qUnion([Q0]), "operationType" : NewBodyOperationType.ADD, "depth" : 4 * mm});
        }
        {
            var Q0;
            {var subQ67=sQuery(id+"F0.wireOp",EDGE,"E0.left");var subQ68=sQuery(id+"F0.wireOp",EDGE,"E0.top");Q0=makeQuery(id+"F5.boolean.opBoolean","SPLIT",FACE,{"disambiguationData":[TD([makeQuery(id+"F1.opExtrude","SWEPT_FACE",FACE,{"disambiguationData":[OSD([subQ67])]})])],"derivedFrom":makeQuery(id+"F1.opExtrude","SWEPT_FACE",FACE,{"disambiguationData":[OSD([subQ68])]})});}
            var sketch = newSketch(context, id + "F17", { "sketchPlane" : qUnion([Q0])});
            skLineSegment(sketch, "E88.bottom", {"start": v(-117.98, 0) * mm, "end": v(-121.98, 0) * mm, "construction": true});
            skLineSegment(sketch, "E88.top", {"start": v(-117.98, 4) * mm, "end": v(-121.98, 4) * mm, "construction": true});
            skLineSegment(sketch, "E88.left", {"start": v(-117.98, 0) * mm, "end": v(-117.98, 4) * mm, "construction": true});
            skLineSegment(sketch, "E88.right", {"start": v(-121.98, 0) * mm, "end": v(-121.98, 4) * mm});
            skLineSegment(sketch, "E89.bottom", {"start": v(-121.98, 0) * mm, "end": v(-124.98, 0) * mm});
            skLineSegment(sketch, "E89.top", {"start": v(-121.98, 4) * mm, "end": v(-124.98, 4) * mm, "construction": true});
            skLineSegment(sketch, "E89.left", {"start": v(-121.98, 0) * mm, "end": v(-121.98, 4) * mm, "construction": true});
            skLineSegment(sketch, "E89.right", {"start": v(-124.98, 0) * mm, "end": v(-124.98, 4) * mm, "construction": true});
            skLineSegment(sketch, "E90.bottom", {"start": v(-157.98, 0) * mm, "end": v(-139.98, 0) * mm, "construction": true});
            skLineSegment(sketch, "E90.top", {"start": v(-157.98, 4) * mm, "end": v(-139.98, 4) * mm, "construction": true});
            skLineSegment(sketch, "E90.left", {"start": v(-157.98, 0) * mm, "end": v(-157.98, 4) * mm, "construction": true});
            skLineSegment(sketch, "E90.right", {"start": v(-139.98, 0) * mm, "end": v(-139.98, 4) * mm, "construction": true});
            skLineSegment(sketch, "E91.bottom", {"start": v(-139.98, 4) * mm, "end": v(-124.98, 4) * mm});
            skLineSegment(sketch, "E91.top", {"start": v(-139.98, 0) * mm, "end": v(-124.98, 0) * mm});
            skLineSegment(sketch, "E91.left", {"start": v(-139.98, 4) * mm, "end": v(-139.98, 0) * mm});
            skLineSegment(sketch, "E91.right", {"start": v(-124.98, 4) * mm, "end": v(-124.98, 0) * mm});
            skSolve(sketch);
        }
        {
            var Q0;
            Q0 = qSketchRegion(id + "F17", true);
            extrude(context, id + "F18", {"entities" : qUnion([Q0]), "operationType" : NewBodyOperationType.REMOVE, "oppositeDirection" : true, "depth" : 4 * mm});
        }
        {
            var Q0;
            Q0=makeQuery(id+"F1.opExtrude","CAP_FACE",FACE,{"disambiguationData":[OSD([sQuery(id+"F0.wireOp",EDGE,"E0.bottom"),sQuery(id+"F0.wireOp",EDGE,"E0.top"),sQuery(id+"F0.wireOp",EDGE,"E0.left"),sQuery(id+"F0.wireOp",EDGE,"E0.right"),sQuery(id+"F0.wireOp",EDGE,"E6.top"),sQuery(id+"F0.wireOp",EDGE,"E6.left"),sQuery(id+"F0.wireOp",EDGE,"E6.right"),sQuery(id+"F0.wireOp",EDGE,"E7.MirrorCS"),sQuery(id+"F0.wireOp",EDGE,"E8.MirrorCS"),sQuery(id+"F0.wireOp",EDGE,"E9.MirrorCS"),sQuery(id+"F0.wireOp",EDGE,"E12.MirrorCS"),sQuery(id+"F0.wireOp",EDGE,"E13.MirrorCS"),sQuery(id+"F0.wireOp",EDGE,"E14.MirrorCS"),sQuery(id+"F0.wireOp",EDGE,"E15.MirrorCS"),sQuery(id+"F0.wireOp",EDGE,"E16.MirrorCS"),sQuery(id+"F0.wireOp",EDGE,"E17.MirrorCS"),sQuery(id+"F0.wireOp",EDGE,"E18.MirrorCS"),sQuery(id+"F0.wireOp",EDGE,"E19.MirrorCS"),sQuery(id+"F0.wireOp",EDGE,"E20.MirrorCS"),sQuery(id+"F0.wireOp",EDGE,"E21.MirrorCS"),sQuery(id+"F0.wireOp",EDGE,"E22.MirrorCS"),sQuery(id+"F0.wireOp",EDGE,"E23.MirrorCS"),sQuery(id+"F0.wireOp",EDGE,"E24.MirrorCS"),sQuery(id+"F0.wireOp",EDGE,"E25.MirrorCS"),sQuery(id+"F0.wireOp",EDGE,"E27.MirrorCS"),sQuery(id+"F0.wireOp",EDGE,"E28.MirrorCS"),sQuery(id+"F0.wireOp",EDGE,"E29.MirrorCS"),sQuery(id+"F0.wireOp",EDGE,"E30.MirrorCS"),sQuery(id+"F0.wireOp",EDGE,"E31.bottom"),sQuery(id+"F0.wireOp",EDGE,"E31.top"),sQuery(id+"F0.wireOp",EDGE,"E31.right"),sQuery(id+"F0.wireOp",EDGE,"E32.MirrorCS"),sQuery(id+"F0.wireOp",EDGE,"E33.MirrorCS"),sQuery(id+"F0.wireOp",EDGE,"E34.MirrorCS"),sQuery(id+"F0.wireOp",EDGE,"E36.1.0.0"),sQuery(id+"F0.wireOp",EDGE,"E36.1.0.1"),sQuery(id+"F0.wireOp",EDGE,"E36.1.0.2"),sQuery(id+"F0.wireOp",EDGE,"E36.1.0.3"),sQuery(id+"F0.wireOp",EDGE,"E36.1.0.4"),sQuery(id+"F0.wireOp",EDGE,"E36.1.0.5"),sQuery(id+"F0.wireOp",EDGE,"E36.2.0.0"),sQuery(id+"F0.wireOp",EDGE,"E36.2.0.1"),sQuery(id+"F0.wireOp",EDGE,"E36.2.0.2"),sQuery(id+"F0.wireOp",EDGE,"E36.2.0.3"),sQuery(id+"F0.wireOp",EDGE,"E36.2.0.4"),sQuery(id+"F0.wireOp",EDGE,"E36.2.0.5"),sQuery(id+"F0.wireOp",EDGE,"E38.MirrorCS"),sQuery(id+"F0.wireOp",EDGE,"E39.MirrorCS"),sQuery(id+"F0.wireOp",EDGE,"E40.MirrorCS"),sQuery(id+"F0.wireOp",EDGE,"E41.MirrorCS"),sQuery(id+"F0.wireOp",EDGE,"E42.MirrorCS"),sQuery(id+"F0.wireOp",EDGE,"E43.MirrorCS"),sQuery(id+"F0.wireOp",EDGE,"E44.MirrorCS"),sQuery(id+"F0.wireOp",EDGE,"E45.MirrorCS"),sQuery(id+"F0.wireOp",EDGE,"E46.MirrorCS"),sQuery(id+"F0.wireOp",EDGE,"E48.MirrorCS"),sQuery(id+"F0.wireOp",EDGE,"E49.MirrorCS"),sQuery(id+"F0.wireOp",EDGE,"E50.MirrorCS"),sQuery(id+"F0.wireOp",EDGE,"E52.MirrorCS"),sQuery(id+"F0.wireOp",EDGE,"E53.MirrorCS"),sQuery(id+"F0.wireOp",EDGE,"E54.MirrorCS"),sQuery(id+"F0.wireOp",EDGE,"E55.MirrorCS"),sQuery(id+"F0.wireOp",EDGE,"E56.MirrorCS"),sQuery(id+"F0.wireOp",EDGE,"E57.MirrorCS"),sQuery(id+"F0.wireOp",EDGE,"E60.MirrorCS"),sQuery(id+"F0.wireOp",EDGE,"E61.MirrorCS"),sQuery(id+"F0.wireOp",EDGE,"E58.MirrorCS"),sQuery(id+"F0.wireOp",EDGE,"E62.MirrorCS"),sQuery(id+"F0.wireOp",EDGE,"E59.MirrorCS"),sQuery(id+"F0.wireOp",EDGE,"E63.MirrorCS")])],"isStart":false});
            var sketch = newSketch(context, id + "F19", { "sketchPlane" : qUnion([Q0])});
            skLineSegment(sketch, "E92.bottom", {"start": v(-117.98, -166.48) * mm, "end": v(-121.98, -166.48) * mm});
            skLineSegment(sketch, "E92.top", {"start": v(-117.98, -146.48) * mm, "end": v(-121.98, -146.48) * mm});
            skLineSegment(sketch, "E92.left", {"start": v(-117.98, -166.48) * mm, "end": v(-117.98, -146.48) * mm});
            skLineSegment(sketch, "E92.right", {"start": v(-121.98, -166.48) * mm, "end": v(-121.98, -146.48) * mm});
            skLineSegment(sketch, "E93.0.1.0", {"start": v(-117.73, -106.49) * mm, "end": v(-121.73, -106.49) * mm});
            skLineSegment(sketch, "E93.0.1.1", {"start": v(-121.73, -126.49) * mm, "end": v(-121.73, -106.49) * mm});
            skLineSegment(sketch, "E93.0.1.2", {"start": v(-117.73, -126.49) * mm, "end": v(-117.73, -106.49) * mm});
            skLineSegment(sketch, "E93.0.1.3", {"start": v(-117.73, -126.49) * mm, "end": v(-121.73, -126.49) * mm});
            skLineSegment(sketch, "E93.direction1", {"start": v(-121.98, -146.48) * mm, "end": v(-96.98, -146.48) * mm, "construction": true});
            skLineSegment(sketch, "E93.direction2", {"start": v(-121.98, -146.48) * mm, "end": v(-121.73, -106.49) * mm, "construction": true});
            skSolve(sketch);
        }
        {
            var Q0;
            Q0 = qSketchRegion(id + "F19", true);
            extrude(context, id + "F20", {"entities" : qUnion([Q0]), "operationType" : NewBodyOperationType.REMOVE, "oppositeDirection" : true, "depth" : 4 * mm});
        }
        {
            var Q0;
            Q0=makeQuery(id+"F1.opExtrude","CAP_FACE",FACE,{"disambiguationData":[OSD([sQuery(id+"F0.wireOp",EDGE,"E0.bottom"),sQuery(id+"F0.wireOp",EDGE,"E0.top"),sQuery(id+"F0.wireOp",EDGE,"E0.left"),sQuery(id+"F0.wireOp",EDGE,"E0.right"),sQuery(id+"F0.wireOp",EDGE,"E6.top"),sQuery(id+"F0.wireOp",EDGE,"E6.left"),sQuery(id+"F0.wireOp",EDGE,"E6.right"),sQuery(id+"F0.wireOp",EDGE,"E7.MirrorCS"),sQuery(id+"F0.wireOp",EDGE,"E8.MirrorCS"),sQuery(id+"F0.wireOp",EDGE,"E9.MirrorCS"),sQuery(id+"F0.wireOp",EDGE,"E12.MirrorCS"),sQuery(id+"F0.wireOp",EDGE,"E13.MirrorCS"),sQuery(id+"F0.wireOp",EDGE,"E14.MirrorCS"),sQuery(id+"F0.wireOp",EDGE,"E15.MirrorCS"),sQuery(id+"F0.wireOp",EDGE,"E16.MirrorCS"),sQuery(id+"F0.wireOp",EDGE,"E17.MirrorCS"),sQuery(id+"F0.wireOp",EDGE,"E18.MirrorCS"),sQuery(id+"F0.wireOp",EDGE,"E19.MirrorCS"),sQuery(id+"F0.wireOp",EDGE,"E20.MirrorCS"),sQuery(id+"F0.wireOp",EDGE,"E21.MirrorCS"),sQuery(id+"F0.wireOp",EDGE,"E22.MirrorCS"),sQuery(id+"F0.wireOp",EDGE,"E23.MirrorCS"),sQuery(id+"F0.wireOp",EDGE,"E24.MirrorCS"),sQuery(id+"F0.wireOp",EDGE,"E25.MirrorCS"),sQuery(id+"F0.wireOp",EDGE,"E27.MirrorCS"),sQuery(id+"F0.wireOp",EDGE,"E28.MirrorCS"),sQuery(id+"F0.wireOp",EDGE,"E29.MirrorCS"),sQuery(id+"F0.wireOp",EDGE,"E30.MirrorCS"),sQuery(id+"F0.wireOp",EDGE,"E31.bottom"),sQuery(id+"F0.wireOp",EDGE,"E31.top"),sQuery(id+"F0.wireOp",EDGE,"E31.right"),sQuery(id+"F0.wireOp",EDGE,"E32.MirrorCS"),sQuery(id+"F0.wireOp",EDGE,"E33.MirrorCS"),sQuery(id+"F0.wireOp",EDGE,"E34.MirrorCS"),sQuery(id+"F0.wireOp",EDGE,"E36.1.0.0"),sQuery(id+"F0.wireOp",EDGE,"E36.1.0.1"),sQuery(id+"F0.wireOp",EDGE,"E36.1.0.2"),sQuery(id+"F0.wireOp",EDGE,"E36.1.0.3"),sQuery(id+"F0.wireOp",EDGE,"E36.1.0.4"),sQuery(id+"F0.wireOp",EDGE,"E36.1.0.5"),sQuery(id+"F0.wireOp",EDGE,"E36.2.0.0"),sQuery(id+"F0.wireOp",EDGE,"E36.2.0.1"),sQuery(id+"F0.wireOp",EDGE,"E36.2.0.2"),sQuery(id+"F0.wireOp",EDGE,"E36.2.0.3"),sQuery(id+"F0.wireOp",EDGE,"E36.2.0.4"),sQuery(id+"F0.wireOp",EDGE,"E36.2.0.5"),sQuery(id+"F0.wireOp",EDGE,"E38.MirrorCS"),sQuery(id+"F0.wireOp",EDGE,"E39.MirrorCS"),sQuery(id+"F0.wireOp",EDGE,"E40.MirrorCS"),sQuery(id+"F0.wireOp",EDGE,"E41.MirrorCS"),sQuery(id+"F0.wireOp",EDGE,"E42.MirrorCS"),sQuery(id+"F0.wireOp",EDGE,"E43.MirrorCS"),sQuery(id+"F0.wireOp",EDGE,"E44.MirrorCS"),sQuery(id+"F0.wireOp",EDGE,"E45.MirrorCS"),sQuery(id+"F0.wireOp",EDGE,"E46.MirrorCS"),sQuery(id+"F0.wireOp",EDGE,"E48.MirrorCS"),sQuery(id+"F0.wireOp",EDGE,"E49.MirrorCS"),sQuery(id+"F0.wireOp",EDGE,"E50.MirrorCS"),sQuery(id+"F0.wireOp",EDGE,"E52.MirrorCS"),sQuery(id+"F0.wireOp",EDGE,"E53.MirrorCS"),sQuery(id+"F0.wireOp",EDGE,"E54.MirrorCS"),sQuery(id+"F0.wireOp",EDGE,"E55.MirrorCS"),sQuery(id+"F0.wireOp",EDGE,"E56.MirrorCS"),sQuery(id+"F0.wireOp",EDGE,"E57.MirrorCS"),sQuery(id+"F0.wireOp",EDGE,"E60.MirrorCS"),sQuery(id+"F0.wireOp",EDGE,"E61.MirrorCS"),sQuery(id+"F0.wireOp",EDGE,"E58.MirrorCS"),sQuery(id+"F0.wireOp",EDGE,"E62.MirrorCS"),sQuery(id+"F0.wireOp",EDGE,"E59.MirrorCS"),sQuery(id+"F0.wireOp",EDGE,"E63.MirrorCS")])],"isStart":false});
            var sketch = newSketch(context, id + "F21", { "sketchPlane" : qUnion([Q0])});
            skLineSegment(sketch, "E94.bottom", {"start": v(2.02, -166.48) * mm, "end": v(9.02, -166.48) * mm, "construction": true});
            skLineSegment(sketch, "E94.top", {"start": v(2.02, -162.48) * mm, "end": v(9.02, -162.48) * mm, "construction": true});
            skLineSegment(sketch, "E94.left", {"start": v(2.02, -166.48) * mm, "end": v(2.02, -162.48) * mm, "construction": true});
            skLineSegment(sketch, "E94.right", {"start": v(9.02, -166.48) * mm, "end": v(9.02, -162.48) * mm, "construction": true});
            skLineSegment(sketch, "E95.bottom", {"start": v(9.02, -162.48) * mm, "end": v(27.02, -162.48) * mm});
            skLineSegment(sketch, "E95.top", {"start": v(9.02, -166.48) * mm, "end": v(27.02, -166.48) * mm});
            skLineSegment(sketch, "E95.left", {"start": v(9.02, -162.48) * mm, "end": v(9.02, -166.48) * mm});
            skLineSegment(sketch, "E95.right", {"start": v(27.02, -162.48) * mm, "end": v(27.02, -166.48) * mm});
            skLineSegment(sketch, "E96.bottom", {"start": v(2.02, -166.48) * mm, "end": v(6.02, -166.48) * mm});
            skLineSegment(sketch, "E96.top", {"start": v(2.02, -146.48) * mm, "end": v(6.02, -146.48) * mm});
            skLineSegment(sketch, "E96.left", {"start": v(2.02, -166.48) * mm, "end": v(2.02, -146.48) * mm});
            skLineSegment(sketch, "E96.right", {"start": v(6.02, -166.48) * mm, "end": v(6.02, -146.48) * mm});
            skLineSegment(sketch, "E97.0.1.0", {"start": v(2.02, -106.48) * mm, "end": v(6.02, -106.48) * mm});
            skLineSegment(sketch, "E97.0.1.1", {"start": v(2.02, -126.48) * mm, "end": v(2.02, -106.48) * mm});
            skLineSegment(sketch, "E97.0.1.2", {"start": v(6.02, -126.48) * mm, "end": v(6.02, -106.48) * mm});
            skLineSegment(sketch, "E97.direction1", {"start": v(2.02, -146.48) * mm, "end": v(27.02, -146.48) * mm, "construction": true});
            skLineSegment(sketch, "E97.direction2", {"start": v(2.02, -146.48) * mm, "end": v(2.02, -106.48) * mm, "construction": true});
            skLineSegment(sketch, "E98", {"start": v(2.02, -126.48) * mm, "end": v(6.02, -126.48) * mm});
            skSolve(sketch);
        }
        {
            var Q0;
            Q0 = qSketchRegion(id + "F21", true);
            extrude(context, id + "F22", {"entities" : qUnion([Q0]), "operationType" : NewBodyOperationType.REMOVE, "oppositeDirection" : true, "depth" : 4 * mm});
        }
        {
            var Q0;
            Q0=makeQuery(id+"F16.boolean.opBoolean","MERGE",FACE,{"derivedFrom":[makeQuery(id+"F12.boolean.opBoolean","MERGE",FACE,{"derivedFrom":[makeQuery(id+"F3.opExtrude","SWEPT_FACE",FACE,{"disambiguationData":[OSD([sQuery(id+"F2.wireOp",EDGE,"E65.0.1.2")])]}),makeQuery(id+"F3.opExtrude","SWEPT_FACE",FACE,{"disambiguationData":[OSD([sQuery(id+"F2.wireOp",EDGE,"E65.0.2.2")])]}),makeQuery(id+"F8.opBoolean","MERGE",FACE,{"derivedFrom":[makeQuery(id+"F3.opExtrude","SWEPT_FACE",FACE,{"disambiguationData":[OSD([sQuery(id+"F2.wireOp",EDGE,"E66.left")])]}),makeQuery(id+"F7.opExtrude","SWEPT_FACE",FACE,{"disambiguationData":[OSD([sQuery(id+"F6.wireOp",EDGE,"E76.left")])]})]}),makeQuery(id+"F9.opBoolean","MERGE",FACE,{"derivedFrom":[makeQuery(id+"F3.opExtrude","SWEPT_FACE",FACE,{"disambiguationData":[OSD([sQuery(id+"F2.wireOp",EDGE,"E67.left")])]}),makeQuery(id+"F7.opExtrude","SWEPT_FACE",FACE,{"disambiguationData":[OSD([sQuery(id+"F6.wireOp",EDGE,"E77.left")])]})]}),makeQuery(id+"F10.opBoolean","MERGE",FACE,{"derivedFrom":[makeQuery(id+"F3.opExtrude","SWEPT_FACE",FACE,{"disambiguationData":[OSD([sQuery(id+"F2.wireOp",EDGE,"E64.left")])]}),makeQuery(id+"F7.opExtrude","SWEPT_FACE",FACE,{"disambiguationData":[OSD([sQuery(id+"F6.wireOp",EDGE,"E75.left")])]})]}),makeQuery(id+"F12.opExtrude","SWEPT_FACE",FACE,{"disambiguationData":[OSD([sQuery(id+"F11.wireOp",EDGE,"E80.left")])]})]}),makeQuery(id+"F16.opExtrude","SWEPT_FACE",FACE,{"disambiguationData":[OSD([sQuery(id+"F15.wireOp",EDGE,"E84.left"),sQuery(id+"F15.wireOp",EDGE,"E86.MirrorCS")])]})]});
            var sketch = newSketch(context, id + "F23", { "sketchPlane" : qUnion([Q0])});
            skLineSegment(sketch, "E99.0", {"start": v(89.48, 58) * mm, "end": v(109.48, 58) * mm});
            skLineSegment(sketch, "E100.0", {"start": v(-33.52, 0) * mm, "end": v(166.48, 0) * mm});
            skSolve(sketch);
        }
        {
            var Q0;
            Q0=makeQuery(id+"F1.opExtrude","CAP_FACE",FACE,{"disambiguationData":[OSD([sQuery(id+"F0.wireOp",EDGE,"E0.bottom"),sQuery(id+"F0.wireOp",EDGE,"E0.top"),sQuery(id+"F0.wireOp",EDGE,"E0.left"),sQuery(id+"F0.wireOp",EDGE,"E0.right"),sQuery(id+"F0.wireOp",EDGE,"E6.top"),sQuery(id+"F0.wireOp",EDGE,"E6.left"),sQuery(id+"F0.wireOp",EDGE,"E6.right"),sQuery(id+"F0.wireOp",EDGE,"E7.MirrorCS"),sQuery(id+"F0.wireOp",EDGE,"E8.MirrorCS"),sQuery(id+"F0.wireOp",EDGE,"E9.MirrorCS"),sQuery(id+"F0.wireOp",EDGE,"E12.MirrorCS"),sQuery(id+"F0.wireOp",EDGE,"E13.MirrorCS"),sQuery(id+"F0.wireOp",EDGE,"E14.MirrorCS"),sQuery(id+"F0.wireOp",EDGE,"E15.MirrorCS"),sQuery(id+"F0.wireOp",EDGE,"E16.MirrorCS"),sQuery(id+"F0.wireOp",EDGE,"E17.MirrorCS"),sQuery(id+"F0.wireOp",EDGE,"E18.MirrorCS"),sQuery(id+"F0.wireOp",EDGE,"E19.MirrorCS"),sQuery(id+"F0.wireOp",EDGE,"E20.MirrorCS"),sQuery(id+"F0.wireOp",EDGE,"E21.MirrorCS"),sQuery(id+"F0.wireOp",EDGE,"E22.MirrorCS"),sQuery(id+"F0.wireOp",EDGE,"E23.MirrorCS"),sQuery(id+"F0.wireOp",EDGE,"E24.MirrorCS"),sQuery(id+"F0.wireOp",EDGE,"E25.MirrorCS"),sQuery(id+"F0.wireOp",EDGE,"E27.MirrorCS"),sQuery(id+"F0.wireOp",EDGE,"E28.MirrorCS"),sQuery(id+"F0.wireOp",EDGE,"E29.MirrorCS"),sQuery(id+"F0.wireOp",EDGE,"E30.MirrorCS"),sQuery(id+"F0.wireOp",EDGE,"E31.bottom"),sQuery(id+"F0.wireOp",EDGE,"E31.top"),sQuery(id+"F0.wireOp",EDGE,"E31.right"),sQuery(id+"F0.wireOp",EDGE,"E32.MirrorCS"),sQuery(id+"F0.wireOp",EDGE,"E33.MirrorCS"),sQuery(id+"F0.wireOp",EDGE,"E34.MirrorCS"),sQuery(id+"F0.wireOp",EDGE,"E36.1.0.0"),sQuery(id+"F0.wireOp",EDGE,"E36.1.0.1"),sQuery(id+"F0.wireOp",EDGE,"E36.1.0.2"),sQuery(id+"F0.wireOp",EDGE,"E36.1.0.3"),sQuery(id+"F0.wireOp",EDGE,"E36.1.0.4"),sQuery(id+"F0.wireOp",EDGE,"E36.1.0.5"),sQuery(id+"F0.wireOp",EDGE,"E36.2.0.0"),sQuery(id+"F0.wireOp",EDGE,"E36.2.0.1"),sQuery(id+"F0.wireOp",EDGE,"E36.2.0.2"),sQuery(id+"F0.wireOp",EDGE,"E36.2.0.3"),sQuery(id+"F0.wireOp",EDGE,"E36.2.0.4"),sQuery(id+"F0.wireOp",EDGE,"E36.2.0.5"),sQuery(id+"F0.wireOp",EDGE,"E38.MirrorCS"),sQuery(id+"F0.wireOp",EDGE,"E39.MirrorCS"),sQuery(id+"F0.wireOp",EDGE,"E40.MirrorCS"),sQuery(id+"F0.wireOp",EDGE,"E41.MirrorCS"),sQuery(id+"F0.wireOp",EDGE,"E42.MirrorCS"),sQuery(id+"F0.wireOp",EDGE,"E43.MirrorCS"),sQuery(id+"F0.wireOp",EDGE,"E44.MirrorCS"),sQuery(id+"F0.wireOp",EDGE,"E45.MirrorCS"),sQuery(id+"F0.wireOp",EDGE,"E46.MirrorCS"),sQuery(id+"F0.wireOp",EDGE,"E48.MirrorCS"),sQuery(id+"F0.wireOp",EDGE,"E49.MirrorCS"),sQuery(id+"F0.wireOp",EDGE,"E50.MirrorCS"),sQuery(id+"F0.wireOp",EDGE,"E52.MirrorCS"),sQuery(id+"F0.wireOp",EDGE,"E53.MirrorCS"),sQuery(id+"F0.wireOp",EDGE,"E54.MirrorCS"),sQuery(id+"F0.wireOp",EDGE,"E55.MirrorCS"),sQuery(id+"F0.wireOp",EDGE,"E56.MirrorCS"),sQuery(id+"F0.wireOp",EDGE,"E57.MirrorCS"),sQuery(id+"F0.wireOp",EDGE,"E60.MirrorCS"),sQuery(id+"F0.wireOp",EDGE,"E61.MirrorCS"),sQuery(id+"F0.wireOp",EDGE,"E58.MirrorCS"),sQuery(id+"F0.wireOp",EDGE,"E62.MirrorCS"),sQuery(id+"F0.wireOp",EDGE,"E59.MirrorCS"),sQuery(id+"F0.wireOp",EDGE,"E63.MirrorCS")])],"isStart":false});
            var sketch = newSketch(context, id + "F24", { "sketchPlane" : qUnion([Q0])});
            skLineSegment(sketch, "E101.0", {"start": v(-117.73, -121.48) * mm, "end": v(-117.73, -106.49) * mm});
            skLineSegment(sketch, "E102.0", {"start": v(2.02, -121.48) * mm, "end": v(2.02, -106.48) * mm});
            skLineSegment(sketch, "E103", {"start": v(-117.73, -106.49) * mm, "end": v(2.02, -106.48) * mm, "construction": true});
            skLineSegment(sketch, "E104.top", {"start": v(-57.85, -111.98) * mm, "end": v(-67.85, -111.98) * mm});
            skLineSegment(sketch, "E104.right", {"start": v(-67.85, -113.98) * mm, "end": v(-67.85, -111.98) * mm});
            skLineSegment(sketch, "E105.MirrorCS", {"start": v(-67.85, -113.98) * mm, "end": v(-67.85, -115.98) * mm});
            skLineSegment(sketch, "E106.MirrorCS", {"start": v(-57.85, -115.98) * mm, "end": v(-67.85, -115.98) * mm});
            skLineSegment(sketch, "E107.MirrorCS", {"start": v(-57.85, -111.98) * mm, "end": v(-47.85, -111.98) * mm});
            skLineSegment(sketch, "E108.MirrorCS", {"start": v(-47.85, -113.98) * mm, "end": v(-47.85, -115.98) * mm});
            skLineSegment(sketch, "E109.MirrorCS", {"start": v(-47.85, -113.98) * mm, "end": v(-47.85, -111.98) * mm});
            skLineSegment(sketch, "E110.MirrorCS", {"start": v(-57.85, -115.98) * mm, "end": v(-47.85, -115.98) * mm});
            skLineSegment(sketch, "E111.1.0.0", {"start": v(-32.85, -113.98) * mm, "end": v(-32.85, -115.98) * mm});
            skLineSegment(sketch, "E111.1.0.1", {"start": v(-32.85, -113.98) * mm, "end": v(-32.85, -111.98) * mm});
            skLineSegment(sketch, "E111.1.0.3", {"start": v(-22.85, -111.98) * mm, "end": v(-32.85, -111.98) * mm});
            skLineSegment(sketch, "E111.1.0.4", {"start": v(-22.85, -115.98) * mm, "end": v(-32.85, -115.98) * mm});
            skLineSegment(sketch, "E111.1.0.6", {"start": v(-22.85, -111.98) * mm, "end": v(-12.85, -111.98) * mm});
            skLineSegment(sketch, "E111.1.0.7", {"start": v(-12.85, -113.98) * mm, "end": v(-12.85, -115.98) * mm});
            skLineSegment(sketch, "E111.1.0.8", {"start": v(-12.85, -113.98) * mm, "end": v(-12.85, -111.98) * mm});
            skLineSegment(sketch, "E111.1.0.9", {"start": v(-22.85, -115.98) * mm, "end": v(-12.85, -115.98) * mm});
            skLineSegment(sketch, "E111.direction1", {"start": v(-67.85, -115.98) * mm, "end": v(-32.85, -115.98) * mm, "construction": true});
            skLineSegment(sketch, "E112.1.0.0", {"start": v(-92.85, -115.98) * mm, "end": v(-102.85, -115.98) * mm});
            skLineSegment(sketch, "E112.1.0.2", {"start": v(-92.85, -111.98) * mm, "end": v(-82.85, -111.98) * mm});
            skLineSegment(sketch, "E112.1.0.3", {"start": v(-82.85, -113.98) * mm, "end": v(-82.85, -111.98) * mm});
            skLineSegment(sketch, "E112.1.0.4", {"start": v(-102.85, -113.98) * mm, "end": v(-102.85, -111.98) * mm});
            skLineSegment(sketch, "E112.1.0.5", {"start": v(-82.85, -113.98) * mm, "end": v(-82.85, -115.98) * mm});
            skLineSegment(sketch, "E112.1.0.6", {"start": v(-92.85, -111.98) * mm, "end": v(-102.85, -111.98) * mm});
            skLineSegment(sketch, "E112.1.0.7", {"start": v(-92.85, -115.98) * mm, "end": v(-82.85, -115.98) * mm});
            skLineSegment(sketch, "E112.1.0.8", {"start": v(-102.85, -113.98) * mm, "end": v(-102.85, -115.98) * mm});
            skLineSegment(sketch, "E112.direction1", {"start": v(-67.85, -115.98) * mm, "end": v(-102.85, -115.98) * mm, "construction": true});
            skSolve(sketch);
        }
        {
            var Q0;
            Q0 = qSketchRegion(id + "F24", true);
            var Q1;
            Q1=makeQuery(id+"F1.opExtrude","CAP_FACE",FACE,{"disambiguationData":[OSD([sQuery(id+"F0.wireOp",EDGE,"E0.bottom"),sQuery(id+"F0.wireOp",EDGE,"E0.top"),sQuery(id+"F0.wireOp",EDGE,"E0.left"),sQuery(id+"F0.wireOp",EDGE,"E0.right"),sQuery(id+"F0.wireOp",EDGE,"E6.top"),sQuery(id+"F0.wireOp",EDGE,"E6.left"),sQuery(id+"F0.wireOp",EDGE,"E6.right"),sQuery(id+"F0.wireOp",EDGE,"E7.MirrorCS"),sQuery(id+"F0.wireOp",EDGE,"E8.MirrorCS"),sQuery(id+"F0.wireOp",EDGE,"E9.MirrorCS"),sQuery(id+"F0.wireOp",EDGE,"E12.MirrorCS"),sQuery(id+"F0.wireOp",EDGE,"E13.MirrorCS"),sQuery(id+"F0.wireOp",EDGE,"E14.MirrorCS"),sQuery(id+"F0.wireOp",EDGE,"E15.MirrorCS"),sQuery(id+"F0.wireOp",EDGE,"E16.MirrorCS"),sQuery(id+"F0.wireOp",EDGE,"E17.MirrorCS"),sQuery(id+"F0.wireOp",EDGE,"E18.MirrorCS"),sQuery(id+"F0.wireOp",EDGE,"E19.MirrorCS"),sQuery(id+"F0.wireOp",EDGE,"E20.MirrorCS"),sQuery(id+"F0.wireOp",EDGE,"E21.MirrorCS"),sQuery(id+"F0.wireOp",EDGE,"E22.MirrorCS"),sQuery(id+"F0.wireOp",EDGE,"E23.MirrorCS"),sQuery(id+"F0.wireOp",EDGE,"E24.MirrorCS"),sQuery(id+"F0.wireOp",EDGE,"E25.MirrorCS"),sQuery(id+"F0.wireOp",EDGE,"E27.MirrorCS"),sQuery(id+"F0.wireOp",EDGE,"E28.MirrorCS"),sQuery(id+"F0.wireOp",EDGE,"E29.MirrorCS"),sQuery(id+"F0.wireOp",EDGE,"E30.MirrorCS"),sQuery(id+"F0.wireOp",EDGE,"E31.bottom"),sQuery(id+"F0.wireOp",EDGE,"E31.top"),sQuery(id+"F0.wireOp",EDGE,"E31.right"),sQuery(id+"F0.wireOp",EDGE,"E32.MirrorCS"),sQuery(id+"F0.wireOp",EDGE,"E33.MirrorCS"),sQuery(id+"F0.wireOp",EDGE,"E34.MirrorCS"),sQuery(id+"F0.wireOp",EDGE,"E36.1.0.0"),sQuery(id+"F0.wireOp",EDGE,"E36.1.0.1"),sQuery(id+"F0.wireOp",EDGE,"E36.1.0.2"),sQuery(id+"F0.wireOp",EDGE,"E36.1.0.3"),sQuery(id+"F0.wireOp",EDGE,"E36.1.0.4"),sQuery(id+"F0.wireOp",EDGE,"E36.1.0.5"),sQuery(id+"F0.wireOp",EDGE,"E36.2.0.0"),sQuery(id+"F0.wireOp",EDGE,"E36.2.0.1"),sQuery(id+"F0.wireOp",EDGE,"E36.2.0.2"),sQuery(id+"F0.wireOp",EDGE,"E36.2.0.3"),sQuery(id+"F0.wireOp",EDGE,"E36.2.0.4"),sQuery(id+"F0.wireOp",EDGE,"E36.2.0.5"),sQuery(id+"F0.wireOp",EDGE,"E38.MirrorCS"),sQuery(id+"F0.wireOp",EDGE,"E39.MirrorCS"),sQuery(id+"F0.wireOp",EDGE,"E40.MirrorCS"),sQuery(id+"F0.wireOp",EDGE,"E41.MirrorCS"),sQuery(id+"F0.wireOp",EDGE,"E42.MirrorCS"),sQuery(id+"F0.wireOp",EDGE,"E43.MirrorCS"),sQuery(id+"F0.wireOp",EDGE,"E44.MirrorCS"),sQuery(id+"F0.wireOp",EDGE,"E45.MirrorCS"),sQuery(id+"F0.wireOp",EDGE,"E46.MirrorCS"),sQuery(id+"F0.wireOp",EDGE,"E48.MirrorCS"),sQuery(id+"F0.wireOp",EDGE,"E49.MirrorCS"),sQuery(id+"F0.wireOp",EDGE,"E50.MirrorCS"),sQuery(id+"F0.wireOp",EDGE,"E52.MirrorCS"),sQuery(id+"F0.wireOp",EDGE,"E53.MirrorCS"),sQuery(id+"F0.wireOp",EDGE,"E54.MirrorCS"),sQuery(id+"F0.wireOp",EDGE,"E55.MirrorCS"),sQuery(id+"F0.wireOp",EDGE,"E56.MirrorCS"),sQuery(id+"F0.wireOp",EDGE,"E57.MirrorCS"),sQuery(id+"F0.wireOp",EDGE,"E60.MirrorCS"),sQuery(id+"F0.wireOp",EDGE,"E61.MirrorCS"),sQuery(id+"F0.wireOp",EDGE,"E58.MirrorCS"),sQuery(id+"F0.wireOp",EDGE,"E62.MirrorCS"),sQuery(id+"F0.wireOp",EDGE,"E59.MirrorCS"),sQuery(id+"F0.wireOp",EDGE,"E63.MirrorCS")])],"isStart":true});
            extrude(context, id + "F25", {"entities" : qUnion([Q0]), "operationType" : NewBodyOperationType.REMOVE, "endBound" : BoundingType.UP_TO_SURFACE, "oppositeDirection" : true, "endBoundEntityFace" : qUnion([Q1]), "depth" : 25 * mm});
        }
        {
            var Q0;
            Q0=makeQuery(id+"F3.opExtrude","SWEPT_FACE",FACE,{"disambiguationData":[OSD([sQuery(id+"F2.wireOp",EDGE,"E65.0.2.0")])]});
            var sketch = newSketch(context, id + "F26", { "sketchPlane" : qUnion([Q0])});
            skLineSegment(sketch, "E113.bottom", {"start": v(143.98, 58) * mm, "end": v(147.98, 58) * mm});
            skLineSegment(sketch, "E113.top", {"start": v(143.98, 27) * mm, "end": v(147.98, 27) * mm});
            skLineSegment(sketch, "E113.left", {"start": v(143.98, 58) * mm, "end": v(143.98, 27) * mm});
            skLineSegment(sketch, "E113.right", {"start": v(147.98, 58) * mm, "end": v(147.98, 27) * mm});
            skSolve(sketch);
        }
        {
            var Q0;
            Q0 = qSketchRegion(id + "F26", true);
            extrude(context, id + "F27", {"entities" : qUnion([Q0]), "operationType" : NewBodyOperationType.ADD, "depth" : 10 * mm});
        }
        {
            var Q0;
            Q0=makeQuery(id+"F1.opExtrude","CAP_FACE",FACE,{"disambiguationData":[OSD([sQuery(id+"F0.wireOp",EDGE,"E0.bottom"),sQuery(id+"F0.wireOp",EDGE,"E0.top"),sQuery(id+"F0.wireOp",EDGE,"E0.left"),sQuery(id+"F0.wireOp",EDGE,"E0.right"),sQuery(id+"F0.wireOp",EDGE,"E6.top"),sQuery(id+"F0.wireOp",EDGE,"E6.left"),sQuery(id+"F0.wireOp",EDGE,"E6.right"),sQuery(id+"F0.wireOp",EDGE,"E7.MirrorCS"),sQuery(id+"F0.wireOp",EDGE,"E8.MirrorCS"),sQuery(id+"F0.wireOp",EDGE,"E9.MirrorCS"),sQuery(id+"F0.wireOp",EDGE,"E12.MirrorCS"),sQuery(id+"F0.wireOp",EDGE,"E13.MirrorCS"),sQuery(id+"F0.wireOp",EDGE,"E14.MirrorCS"),sQuery(id+"F0.wireOp",EDGE,"E15.MirrorCS"),sQuery(id+"F0.wireOp",EDGE,"E16.MirrorCS"),sQuery(id+"F0.wireOp",EDGE,"E17.MirrorCS"),sQuery(id+"F0.wireOp",EDGE,"E18.MirrorCS"),sQuery(id+"F0.wireOp",EDGE,"E19.MirrorCS"),sQuery(id+"F0.wireOp",EDGE,"E20.MirrorCS"),sQuery(id+"F0.wireOp",EDGE,"E21.MirrorCS"),sQuery(id+"F0.wireOp",EDGE,"E22.MirrorCS"),sQuery(id+"F0.wireOp",EDGE,"E23.MirrorCS"),sQuery(id+"F0.wireOp",EDGE,"E24.MirrorCS"),sQuery(id+"F0.wireOp",EDGE,"E25.MirrorCS"),sQuery(id+"F0.wireOp",EDGE,"E27.MirrorCS"),sQuery(id+"F0.wireOp",EDGE,"E28.MirrorCS"),sQuery(id+"F0.wireOp",EDGE,"E29.MirrorCS"),sQuery(id+"F0.wireOp",EDGE,"E30.MirrorCS"),sQuery(id+"F0.wireOp",EDGE,"E31.bottom"),sQuery(id+"F0.wireOp",EDGE,"E31.top"),sQuery(id+"F0.wireOp",EDGE,"E31.right"),sQuery(id+"F0.wireOp",EDGE,"E32.MirrorCS"),sQuery(id+"F0.wireOp",EDGE,"E33.MirrorCS"),sQuery(id+"F0.wireOp",EDGE,"E34.MirrorCS"),sQuery(id+"F0.wireOp",EDGE,"E36.1.0.0"),sQuery(id+"F0.wireOp",EDGE,"E36.1.0.1"),sQuery(id+"F0.wireOp",EDGE,"E36.1.0.2"),sQuery(id+"F0.wireOp",EDGE,"E36.1.0.3"),sQuery(id+"F0.wireOp",EDGE,"E36.1.0.4"),sQuery(id+"F0.wireOp",EDGE,"E36.1.0.5"),sQuery(id+"F0.wireOp",EDGE,"E36.2.0.0"),sQuery(id+"F0.wireOp",EDGE,"E36.2.0.1"),sQuery(id+"F0.wireOp",EDGE,"E36.2.0.2"),sQuery(id+"F0.wireOp",EDGE,"E36.2.0.3"),sQuery(id+"F0.wireOp",EDGE,"E36.2.0.4"),sQuery(id+"F0.wireOp",EDGE,"E36.2.0.5"),sQuery(id+"F0.wireOp",EDGE,"E38.MirrorCS"),sQuery(id+"F0.wireOp",EDGE,"E39.MirrorCS"),sQuery(id+"F0.wireOp",EDGE,"E40.MirrorCS"),sQuery(id+"F0.wireOp",EDGE,"E41.MirrorCS"),sQuery(id+"F0.wireOp",EDGE,"E42.MirrorCS"),sQuery(id+"F0.wireOp",EDGE,"E43.MirrorCS"),sQuery(id+"F0.wireOp",EDGE,"E44.MirrorCS"),sQuery(id+"F0.wireOp",EDGE,"E45.MirrorCS"),sQuery(id+"F0.wireOp",EDGE,"E46.MirrorCS"),sQuery(id+"F0.wireOp",EDGE,"E48.MirrorCS"),sQuery(id+"F0.wireOp",EDGE,"E49.MirrorCS"),sQuery(id+"F0.wireOp",EDGE,"E50.MirrorCS"),sQuery(id+"F0.wireOp",EDGE,"E52.MirrorCS"),sQuery(id+"F0.wireOp",EDGE,"E53.MirrorCS"),sQuery(id+"F0.wireOp",EDGE,"E54.MirrorCS"),sQuery(id+"F0.wireOp",EDGE,"E55.MirrorCS"),sQuery(id+"F0.wireOp",EDGE,"E56.MirrorCS"),sQuery(id+"F0.wireOp",EDGE,"E57.MirrorCS"),sQuery(id+"F0.wireOp",EDGE,"E60.MirrorCS"),sQuery(id+"F0.wireOp",EDGE,"E61.MirrorCS"),sQuery(id+"F0.wireOp",EDGE,"E58.MirrorCS"),sQuery(id+"F0.wireOp",EDGE,"E62.MirrorCS"),sQuery(id+"F0.wireOp",EDGE,"E59.MirrorCS"),sQuery(id+"F0.wireOp",EDGE,"E63.MirrorCS")])],"isStart":true});
            var sketch = newSketch(context, id + "F28", { "sketchPlane" : qUnion([Q0])});
            skLineSegment(sketch, "E114.bottom", {"start": v(-147.98, 56.48) * mm, "end": v(-157.98, 56.48) * mm});
            skLineSegment(sketch, "E114.top", {"start": v(-147.98, -23.52) * mm, "end": v(-157.98, -23.52) * mm});
            skLineSegment(sketch, "E114.left", {"start": v(-147.98, 56.48) * mm, "end": v(-147.98, -23.52) * mm});
            skLineSegment(sketch, "E114.right", {"start": v(-157.98, 56.48) * mm, "end": v(-157.98, -23.52) * mm});
            skLineSegment(sketch, "E115.bottom", {"start": v(-147.98, 56.48) * mm, "end": v(-122.98, 56.48) * mm});
            skLineSegment(sketch, "E115.top", {"start": v(-147.98, -23.52) * mm, "end": v(-122.98, -23.52) * mm});
            skLineSegment(sketch, "E115.right", {"start": v(-122.98, 56.48) * mm, "end": v(-122.98, -23.52) * mm});
            skLineSegment(sketch, "E116.bottom", {"start": v(32.02, 56.48) * mm, "end": v(42.02, 56.48) * mm});
            skLineSegment(sketch, "E116.top", {"start": v(32.02, -23.52) * mm, "end": v(42.02, -23.52) * mm});
            skLineSegment(sketch, "E116.left", {"start": v(32.02, 56.48) * mm, "end": v(32.02, -23.52) * mm});
            skLineSegment(sketch, "E116.right", {"start": v(42.02, 56.48) * mm, "end": v(42.02, -23.52) * mm});
            skLineSegment(sketch, "E117.bottom", {"start": v(32.02, -23.52) * mm, "end": v(7.02, -23.52) * mm});
            skLineSegment(sketch, "E117.top", {"start": v(32.02, 56.48) * mm, "end": v(7.02, 56.48) * mm});
            skLineSegment(sketch, "E117.left", {"start": v(32.02, -23.52) * mm, "end": v(32.02, 56.48) * mm});
            skLineSegment(sketch, "E117.right", {"start": v(7.02, -23.52) * mm, "end": v(7.02, 56.48) * mm});
            skSolve(sketch);
        }
        {
            var Q0;
            Q0 = qSketchRegion(id + "F28", true);
            extrude(context, id + "F29", {"entities" : qUnion([Q0]), "operationType" : NewBodyOperationType.REMOVE, "oppositeDirection" : true, "depth" : 25 * mm});
        }
        {
            var Q0;
            Q0=makeQuery(id+"F27.boolean.opBoolean","MERGE",FACE,{"derivedFrom":[makeQuery(id+"F16.boolean.opBoolean","MERGE",FACE,{"derivedFrom":[makeQuery(id+"F12.boolean.opBoolean","MERGE",FACE,{"derivedFrom":[makeQuery(id+"F3.opExtrude","SWEPT_FACE",FACE,{"disambiguationData":[OSD([sQuery(id+"F2.wireOp",EDGE,"E65.0.1.3")])]}),makeQuery(id+"F3.opExtrude","SWEPT_FACE",FACE,{"disambiguationData":[OSD([sQuery(id+"F2.wireOp",EDGE,"E65.0.2.3")])]}),makeQuery(id+"F8.opBoolean","MERGE",FACE,{"derivedFrom":[makeQuery(id+"F3.opExtrude","SWEPT_FACE",FACE,{"disambiguationData":[OSD([sQuery(id+"F2.wireOp",EDGE,"E66.right")])]}),makeQuery(id+"F7.opExtrude","SWEPT_FACE",FACE,{"disambiguationData":[OSD([sQuery(id+"F6.wireOp",EDGE,"E76.right")])]})]}),makeQuery(id+"F9.opBoolean","MERGE",FACE,{"derivedFrom":[makeQuery(id+"F3.opExtrude","SWEPT_FACE",FACE,{"disambiguationData":[OSD([sQuery(id+"F2.wireOp",EDGE,"E67.right")])]}),makeQuery(id+"F7.opExtrude","SWEPT_FACE",FACE,{"disambiguationData":[OSD([sQuery(id+"F6.wireOp",EDGE,"E77.right")])]})]}),makeQuery(id+"F10.opBoolean","MERGE",FACE,{"derivedFrom":[makeQuery(id+"F3.opExtrude","SWEPT_FACE",FACE,{"disambiguationData":[OSD([sQuery(id+"F2.wireOp",EDGE,"E64.right")])]}),makeQuery(id+"F7.opExtrude","SWEPT_FACE",FACE,{"disambiguationData":[OSD([sQuery(id+"F6.wireOp",EDGE,"E75.right")])]})]}),makeQuery(id+"F12.opExtrude","SWEPT_FACE",FACE,{"disambiguationData":[OSD([sQuery(id+"F11.wireOp",EDGE,"E80.right")])]})]}),makeQuery(id+"F16.opExtrude","SWEPT_FACE",FACE,{"disambiguationData":[OSD([sQuery(id+"F15.wireOp",EDGE,"E84.right"),sQuery(id+"F15.wireOp",EDGE,"E87.MirrorCS")])]})]}),makeQuery(id+"F27.opExtrude","SWEPT_FACE",FACE,{"disambiguationData":[OSD([sQuery(id+"F26.wireOp",EDGE,"E113.left")])]})]});
            var sketch = newSketch(context, id + "F30", { "sketchPlane" : qUnion([Q0])});
            skLineSegment(sketch, "E118.bottom", {"start": v(-56.48, 27) * mm, "end": v(23.52, 27) * mm});
            skLineSegment(sketch, "E118.top", {"start": v(-56.48, 58) * mm, "end": v(23.52, 58) * mm});
            skLineSegment(sketch, "E118.left", {"start": v(-56.48, 27) * mm, "end": v(-56.48, 58) * mm});
            skLineSegment(sketch, "E118.right", {"start": v(23.52, 27) * mm, "end": v(23.52, 58) * mm});
            skSolve(sketch);
        }
        {
            var Q0;
            Q0 = qSketchRegion(id + "F30", true);
            extrude(context, id + "F31", {"entities" : qUnion([Q0]), "operationType" : NewBodyOperationType.REMOVE, "oppositeDirection" : true, "depth" : 25 * mm});
        }
    });
